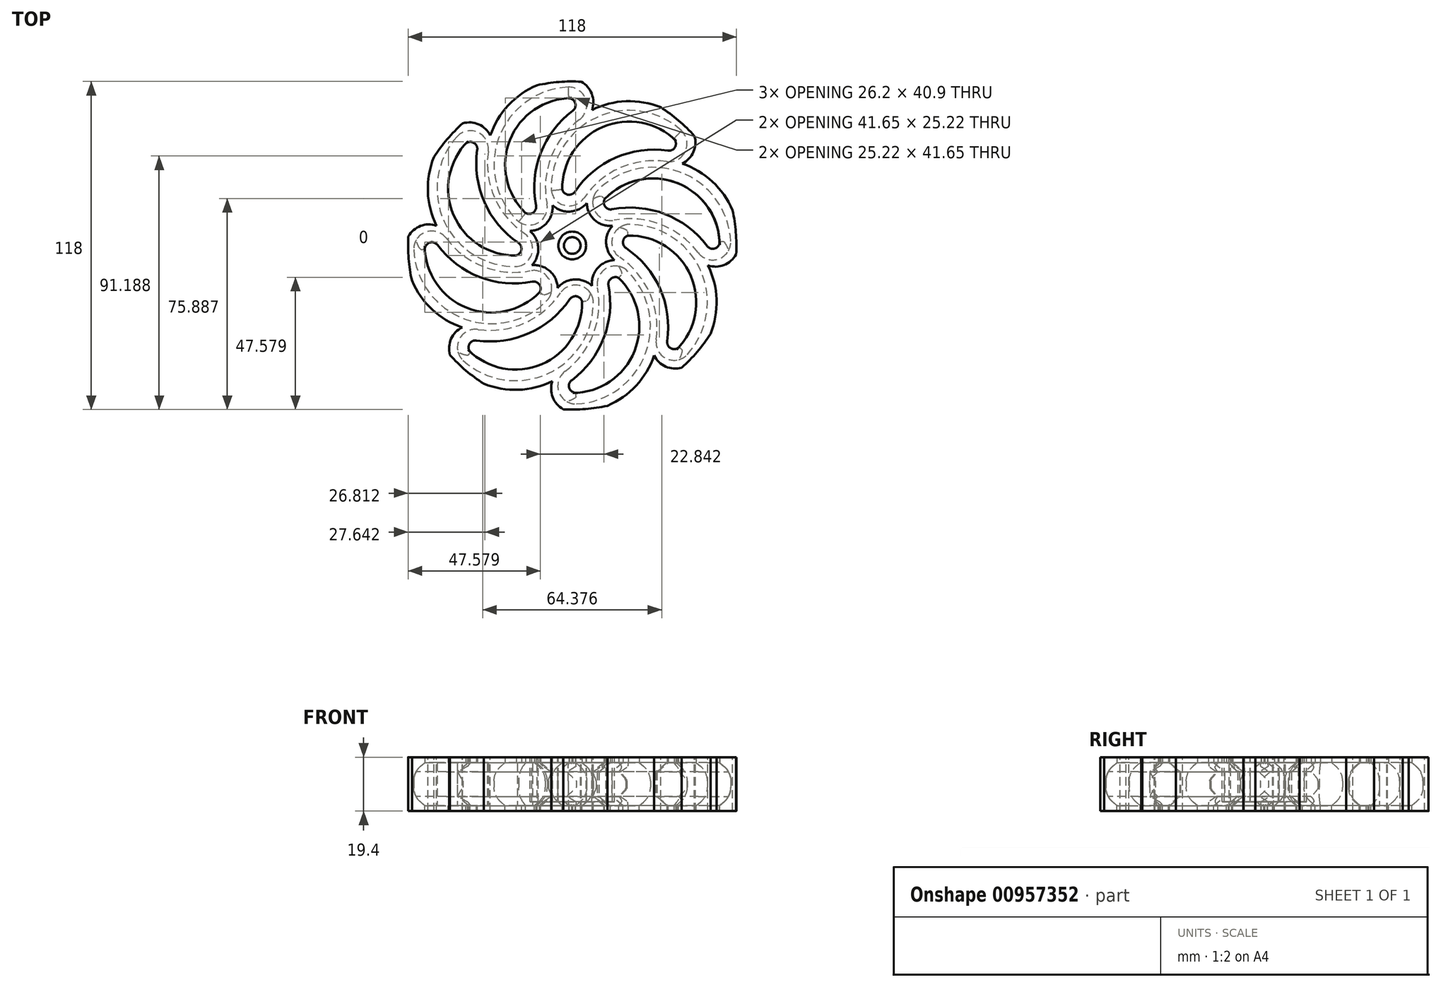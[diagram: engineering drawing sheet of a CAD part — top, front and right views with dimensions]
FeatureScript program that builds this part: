
annotation { "Feature Type Name" : "Feature", "Feature Type Description" : "" }
export const myFeature = defineFeature(function(context is Context, id is Id, definition is map)
    precondition{}
    {
        {
            var Q0;
            Q0=qCreatedBy(makeId("Top.planeOp"),FACE);
            var sketch = newSketch(context, id + "F0", { "sketchPlane" : qUnion([Q0])});
            skCircle(sketch, "E0", {"center": v(0, 0) * mm, "radius": 59 * mm});
            skCircle(sketch, "E1", {"center": v(0, 0) * mm, "radius": 1.5 * mm});
            skLineSegment(sketch, "E2", {"start": v(0, 0) * mm, "end": v(41.72, 41.72) * mm, "construction": true});
            skArc(sketch, "E3", {"start": v(41.72, 41.72) * mm, "mid": v(0, 41.72) * mm, "end": v(0, 0) * mm, "construction": true});
            skCircle(sketch, "E4.0", {"center": v(0, 0) * mm, "radius": 57 * mm});
            skArc(sketch, "E5.0", {"start": v(25.42, 51.02) * mm, "mid": v(-6.1, 35.12) * mm, "end": v(-1.5, 0.11) * mm});
            skArc(sketch, "E6.0", {"start": v(32.3, 46.96) * mm, "mid": v(-2.36, 37.39) * mm, "end": v(-0.05, 1.5) * mm});
            skArc(sketch, "E7.1.0", {"start": v(-18.1, 54.05) * mm, "mid": v(-29.15, 20.52) * mm, "end": v(-1.14, -0.98) * mm});
            skArc(sketch, "E7.1.1", {"start": v(-10.36, 56.05) * mm, "mid": v(-28.1, 24.77) * mm, "end": v(-1.1, 1.02) * mm});
            skArc(sketch, "E7.2.0", {"start": v(-51.02, 25.42) * mm, "mid": v(-35.12, -6.1) * mm, "end": v(-0.11, -1.5) * mm});
            skArc(sketch, "E7.2.1", {"start": v(-46.96, 32.3) * mm, "mid": v(-37.39, -2.36) * mm, "end": v(-1.5, -0.05) * mm});
            skArc(sketch, "E7.3.0", {"start": v(-54.05, -18.1) * mm, "mid": v(-20.52, -29.15) * mm, "end": v(0.98, -1.14) * mm});
            skArc(sketch, "E7.3.1", {"start": v(-56.05, -10.36) * mm, "mid": v(-24.77, -28.1) * mm, "end": v(-1.02, -1.1) * mm});
            skArc(sketch, "E7.4.0", {"start": v(-25.42, -51.02) * mm, "mid": v(6.1, -35.12) * mm, "end": v(1.5, -0.11) * mm});
            skArc(sketch, "E7.4.1", {"start": v(-32.3, -46.96) * mm, "mid": v(2.36, -37.39) * mm, "end": v(0.05, -1.5) * mm});
            skArc(sketch, "E7.5.0", {"start": v(18.1, -54.05) * mm, "mid": v(29.15, -20.52) * mm, "end": v(1.14, 0.98) * mm});
            skArc(sketch, "E7.5.1", {"start": v(10.36, -56.05) * mm, "mid": v(28.1, -24.77) * mm, "end": v(1.1, -1.02) * mm});
            skArc(sketch, "E7.6.0", {"start": v(51.02, -25.42) * mm, "mid": v(35.12, 6.1) * mm, "end": v(0.11, 1.5) * mm});
            skArc(sketch, "E7.6.1", {"start": v(46.96, -32.3) * mm, "mid": v(37.39, 2.36) * mm, "end": v(1.5, 0.05) * mm});
            skArc(sketch, "E7.7.0", {"start": v(54.05, 18.1) * mm, "mid": v(20.52, 29.15) * mm, "end": v(-0.98, 1.14) * mm});
            skArc(sketch, "E7.7.1", {"start": v(56.05, 10.36) * mm, "mid": v(24.77, 28.1) * mm, "end": v(1.02, 1.1) * mm});
            skSolve(sketch);
        }
        {
            var Q0;
            {var subQ7=sQuery(id+"F0.wireOp",EDGE,"E7.1.1");var subQ9=sQuery(id+"F0.wireOp",EDGE,"E1");var subQ10=makeQuery(id+"F0.imprint","INTERSECT",VERTEX,{"derivedFrom":[subQ9,subQ7]});Q0=makeQuery(id+"F0.imprint","IMPRINT",FACE,{"disambiguationData":[TD([[makeQuery(id+"F0.imprint","IMPRINT",EDGE,{"disambiguationData":[TD([[subQ10,1.0]])],"derivedFrom":subQ9}),-1.0]])]});}
            var Q1;
            {var subQ1=sQuery(id+"F0.wireOp",EDGE,"E1");var subQ5=sQuery(id+"F0.wireOp",EDGE,"E6.0");var subQ6=makeQuery(id+"F0.imprint","INTERSECT",VERTEX,{"derivedFrom":[subQ1,subQ5]});Q1=makeQuery(id+"F0.imprint","IMPRINT",FACE,{"disambiguationData":[TD([[makeQuery(id+"F0.imprint","IMPRINT",EDGE,{"disambiguationData":[TD([[subQ6,1.0]])],"derivedFrom":subQ1}),-1.0]])]});}
            var Q2;
            {var subQ0=sQuery(id+"F0.wireOp",EDGE,"E7.5.0");var subQ1=sQuery(id+"F0.wireOp",EDGE,"E1");var subQ2=makeQuery(id+"F0.imprint","INTERSECT",VERTEX,{"derivedFrom":[subQ1,subQ0]});Q2=makeQuery(id+"F0.imprint","IMPRINT",FACE,{"disambiguationData":[TD([[makeQuery(id+"F0.imprint","IMPRINT",EDGE,{"disambiguationData":[TD([[subQ2,-1.0]])],"derivedFrom":subQ1}),-1.0]])]});}
            var Q3;
            {var subQ5=sQuery(id+"F0.wireOp",EDGE,"E7.4.0");var subQ6=sQuery(id+"F0.wireOp",EDGE,"E1");var subQ7=makeQuery(id+"F0.imprint","INTERSECT",VERTEX,{"derivedFrom":[subQ6,subQ5]});Q3=makeQuery(id+"F0.imprint","IMPRINT",FACE,{"disambiguationData":[TD([[makeQuery(id+"F0.imprint","IMPRINT",EDGE,{"disambiguationData":[TD([[subQ7,-1.0]])],"derivedFrom":subQ6}),-1.0]])]});}
            var Q4;
            {var subQ0=sQuery(id+"F0.wireOp",EDGE,"E7.3.0");var subQ1=sQuery(id+"F0.wireOp",EDGE,"E1");var subQ2=makeQuery(id+"F0.imprint","INTERSECT",VERTEX,{"derivedFrom":[subQ1,subQ0]});Q4=makeQuery(id+"F0.imprint","IMPRINT",FACE,{"disambiguationData":[TD([[makeQuery(id+"F0.imprint","IMPRINT",EDGE,{"disambiguationData":[TD([[subQ2,-1.0]])],"derivedFrom":subQ1}),-1.0]])]});}
            var Q5;
            {var subQ5=sQuery(id+"F0.wireOp",EDGE,"E7.2.0");var subQ6=sQuery(id+"F0.wireOp",EDGE,"E1");var subQ7=makeQuery(id+"F0.imprint","INTERSECT",VERTEX,{"derivedFrom":[subQ6,subQ5]});Q5=makeQuery(id+"F0.imprint","IMPRINT",FACE,{"disambiguationData":[TD([[makeQuery(id+"F0.imprint","IMPRINT",EDGE,{"disambiguationData":[TD([[subQ7,-1.0]])],"derivedFrom":subQ6}),-1.0]])]});}
            var Q6;
            {var subQ5=sQuery(id+"F0.wireOp",EDGE,"E7.1.0");var subQ6=sQuery(id+"F0.wireOp",EDGE,"E1");var subQ7=makeQuery(id+"F0.imprint","INTERSECT",VERTEX,{"derivedFrom":[subQ6,subQ5]});Q6=makeQuery(id+"F0.imprint","IMPRINT",FACE,{"disambiguationData":[TD([[makeQuery(id+"F0.imprint","IMPRINT",EDGE,{"disambiguationData":[TD([[subQ7,-1.0]])],"derivedFrom":subQ6}),-1.0]])]});}
            var Q7;
            {var subQ5=sQuery(id+"F0.wireOp",EDGE,"E5.0");var subQ6=sQuery(id+"F0.wireOp",EDGE,"E1");var subQ7=makeQuery(id+"F0.imprint","INTERSECT",VERTEX,{"derivedFrom":[subQ6,subQ5]});Q7=makeQuery(id+"F0.imprint","IMPRINT",FACE,{"disambiguationData":[TD([[makeQuery(id+"F0.imprint","IMPRINT",EDGE,{"disambiguationData":[TD([[subQ7,-1.0]])],"derivedFrom":subQ6}),-1.0]])]});}
            var Q8;
            {var subQ0=sQuery(id+"F0.wireOp",EDGE,"E5.0");var subQ1=sQuery(id+"F0.wireOp",EDGE,"E1");var subQ2=makeQuery(id+"F0.imprint","INTERSECT",VERTEX,{"derivedFrom":[subQ1,subQ0]});Q8=makeQuery(id+"F0.imprint","IMPRINT",FACE,{"disambiguationData":[TD([[makeQuery(id+"F0.imprint","IMPRINT",EDGE,{"disambiguationData":[TD([[subQ2,1.0]])],"derivedFrom":subQ1}),-1.0]])]});}
            var Q9;
            {var subQ0=sQuery(id+"F0.wireOp",EDGE,"E6.0");var subQ1=sQuery(id+"F0.wireOp",EDGE,"E1");var subQ2=makeQuery(id+"F0.imprint","INTERSECT",VERTEX,{"derivedFrom":[subQ1,subQ0]});Q9=makeQuery(id+"F0.imprint","IMPRINT",FACE,{"disambiguationData":[TD([[makeQuery(id+"F0.imprint","IMPRINT",EDGE,{"disambiguationData":[TD([[subQ2,-1.0]])],"derivedFrom":subQ1}),-1.0]])]});}
            var Q10;
            {var subQ0=sQuery(id+"F0.wireOp",EDGE,"E7.6.0");var subQ1=sQuery(id+"F0.wireOp",EDGE,"E1");var subQ2=makeQuery(id+"F0.imprint","INTERSECT",VERTEX,{"derivedFrom":[subQ1,subQ0]});Q10=makeQuery(id+"F0.imprint","IMPRINT",FACE,{"disambiguationData":[TD([[makeQuery(id+"F0.imprint","IMPRINT",EDGE,{"disambiguationData":[TD([[subQ2,1.0]])],"derivedFrom":subQ1}),-1.0]])]});}
            var Q11;
            {var subQ0=sQuery(id+"F0.wireOp",EDGE,"E7.5.0");var subQ1=sQuery(id+"F0.wireOp",EDGE,"E1");var subQ2=makeQuery(id+"F0.imprint","INTERSECT",VERTEX,{"derivedFrom":[subQ1,subQ0]});Q11=makeQuery(id+"F0.imprint","IMPRINT",FACE,{"disambiguationData":[TD([[makeQuery(id+"F0.imprint","IMPRINT",EDGE,{"disambiguationData":[TD([[subQ2,1.0]])],"derivedFrom":subQ1}),-1.0]])]});}
            var Q12;
            {var subQ0=sQuery(id+"F0.wireOp",EDGE,"E7.4.0");var subQ1=sQuery(id+"F0.wireOp",EDGE,"E1");var subQ2=makeQuery(id+"F0.imprint","INTERSECT",VERTEX,{"derivedFrom":[subQ1,subQ0]});Q12=makeQuery(id+"F0.imprint","IMPRINT",FACE,{"disambiguationData":[TD([[makeQuery(id+"F0.imprint","IMPRINT",EDGE,{"disambiguationData":[TD([[subQ2,1.0]])],"derivedFrom":subQ1}),-1.0]])]});}
            var Q13;
            {var subQ0=sQuery(id+"F0.wireOp",EDGE,"E7.3.0");var subQ1=sQuery(id+"F0.wireOp",EDGE,"E1");var subQ2=makeQuery(id+"F0.imprint","INTERSECT",VERTEX,{"derivedFrom":[subQ1,subQ0]});Q13=makeQuery(id+"F0.imprint","IMPRINT",FACE,{"disambiguationData":[TD([[makeQuery(id+"F0.imprint","IMPRINT",EDGE,{"disambiguationData":[TD([[subQ2,1.0]])],"derivedFrom":subQ1}),-1.0]])]});}
            var Q14;
            {var subQ0=sQuery(id+"F0.wireOp",EDGE,"E7.2.0");var subQ1=sQuery(id+"F0.wireOp",EDGE,"E1");var subQ2=makeQuery(id+"F0.imprint","INTERSECT",VERTEX,{"derivedFrom":[subQ1,subQ0]});Q14=makeQuery(id+"F0.imprint","IMPRINT",FACE,{"disambiguationData":[TD([[makeQuery(id+"F0.imprint","IMPRINT",EDGE,{"disambiguationData":[TD([[subQ2,1.0]])],"derivedFrom":subQ1}),-1.0]])]});}
            var Q15;
            {var subQ0=sQuery(id+"F0.wireOp",EDGE,"E7.1.0");var subQ1=sQuery(id+"F0.wireOp",EDGE,"E1");var subQ2=makeQuery(id+"F0.imprint","INTERSECT",VERTEX,{"derivedFrom":[subQ1,subQ0]});Q15=makeQuery(id+"F0.imprint","IMPRINT",FACE,{"disambiguationData":[TD([[makeQuery(id+"F0.imprint","IMPRINT",EDGE,{"disambiguationData":[TD([[subQ2,1.0]])],"derivedFrom":subQ1}),-1.0]])]});}
            var Q16;
            Q16=makeQuery(id+"F0.imprint","IMPRINT",FACE,{"disambiguationData":[TD([[makeQuery(id+"F0.imprint","IMPRINT",EDGE,{"derivedFrom":sQuery(id+"F0.wireOp",EDGE,"E0")}),1.0]])]});
            extrude(context, id + "F1", {"entities" : qUnion([Q0, Q1, Q2, Q3, Q4, Q5, Q6, Q7, Q8, Q9, Q10, Q11, Q12, Q13, Q14, Q15, Q16]), "depth" : 3.1 * mm, "offsetDistance" : 25 * mm, "hasSecondDirection" : true, "secondDirectionOppositeDirection" : true, "secondDirectionDepth" : .4 * mm});
        }
        {
            var Q0;
            Q0=makeQuery(id+"F1.opExtrude","SWEPT_EDGE",EDGE,{"disambiguationData":[OSD([sQuery(id+"F0.wireOp",EDGE,"E7.4.0"),sQuery(id+"F0.wireOp",EDGE,"E7.5.1")])]});
            var Q1;
            Q1=makeQuery(id+"F1.opExtrude","SWEPT_EDGE",EDGE,{"disambiguationData":[OSD([sQuery(id+"F0.wireOp",EDGE,"E7.5.0"),sQuery(id+"F0.wireOp",EDGE,"E7.6.1")])]});
            var Q2;
            Q2=makeQuery(id+"F1.opExtrude","SWEPT_EDGE",EDGE,{"disambiguationData":[OSD([sQuery(id+"F0.wireOp",EDGE,"E7.6.0"),sQuery(id+"F0.wireOp",EDGE,"E7.7.1")])]});
            var Q3;
            Q3=makeQuery(id+"F1.opExtrude","SWEPT_EDGE",EDGE,{"disambiguationData":[OSD([sQuery(id+"F0.wireOp",EDGE,"E6.0"),sQuery(id+"F0.wireOp",EDGE,"E7.7.0")])]});
            var Q4;
            Q4=makeQuery(id+"F1.opExtrude","SWEPT_EDGE",EDGE,{"disambiguationData":[OSD([sQuery(id+"F0.wireOp",EDGE,"E7.1.0"),sQuery(id+"F0.wireOp",EDGE,"E7.2.1")])]});
            var Q5;
            Q5=makeQuery(id+"F1.opExtrude","SWEPT_EDGE",EDGE,{"disambiguationData":[OSD([sQuery(id+"F0.wireOp",EDGE,"E7.2.0"),sQuery(id+"F0.wireOp",EDGE,"E7.3.1")])]});
            var Q6;
            Q6=makeQuery(id+"F1.opExtrude","SWEPT_EDGE",EDGE,{"disambiguationData":[OSD([sQuery(id+"F0.wireOp",EDGE,"E7.3.0"),sQuery(id+"F0.wireOp",EDGE,"E7.4.1")])]});
            var Q7;
            Q7=makeQuery(id+"F1.opExtrude","SWEPT_EDGE",EDGE,{"disambiguationData":[OSD([sQuery(id+"F0.wireOp",EDGE,"E5.0"),sQuery(id+"F0.wireOp",EDGE,"E7.1.1")])]});
            fillet(context, id + "F2", {"entities" : qUnion([Q0, Q1, Q2, Q3, Q4, Q5, Q6, Q7]), "radius" : 6.5 * mm, "tangentPropagation" : true, "allowEdgeOverflow" : false});
        }
        {
            var Q0;
            Q0=makeQuery(id+"F1.opExtrude","SWEPT_EDGE",EDGE,{"disambiguationData":[OSD([sQuery(id+"F0.wireOp",EDGE,"E4.0"),sQuery(id+"F0.wireOp",EDGE,"E7.4.0")])]});
            var Q1;
            Q1=makeQuery(id+"F1.opExtrude","SWEPT_EDGE",EDGE,{"disambiguationData":[OSD([sQuery(id+"F0.wireOp",EDGE,"E4.0"),sQuery(id+"F0.wireOp",EDGE,"E7.3.0")])]});
            var Q2;
            Q2=makeQuery(id+"F1.opExtrude","SWEPT_EDGE",EDGE,{"disambiguationData":[OSD([sQuery(id+"F0.wireOp",EDGE,"E4.0"),sQuery(id+"F0.wireOp",EDGE,"E7.2.0")])]});
            var Q3;
            Q3=makeQuery(id+"F1.opExtrude","SWEPT_EDGE",EDGE,{"disambiguationData":[OSD([sQuery(id+"F0.wireOp",EDGE,"E4.0"),sQuery(id+"F0.wireOp",EDGE,"E7.1.0")])]});
            var Q4;
            Q4=makeQuery(id+"F1.opExtrude","SWEPT_EDGE",EDGE,{"disambiguationData":[OSD([sQuery(id+"F0.wireOp",EDGE,"E4.0"),sQuery(id+"F0.wireOp",EDGE,"E5.0")])]});
            var Q5;
            Q5=makeQuery(id+"F1.opExtrude","SWEPT_EDGE",EDGE,{"disambiguationData":[OSD([sQuery(id+"F0.wireOp",EDGE,"E4.0"),sQuery(id+"F0.wireOp",EDGE,"E7.7.0")])]});
            var Q6;
            Q6=makeQuery(id+"F1.opExtrude","SWEPT_EDGE",EDGE,{"disambiguationData":[OSD([sQuery(id+"F0.wireOp",EDGE,"E4.0"),sQuery(id+"F0.wireOp",EDGE,"E7.6.0")])]});
            var Q7;
            Q7=makeQuery(id+"F1.opExtrude","SWEPT_EDGE",EDGE,{"disambiguationData":[OSD([sQuery(id+"F0.wireOp",EDGE,"E4.0"),sQuery(id+"F0.wireOp",EDGE,"E7.5.0")])]});
            fillet(context, id + "F3", {"entities" : qUnion([Q0, Q1, Q2, Q3, Q4, Q5, Q6, Q7]), "radius" : 6.5 * mm, "tangentPropagation" : true, "allowEdgeOverflow" : false});
        }
        {
            var Q0;
            Q0=makeQuery(id+"F1.opExtrude","SWEPT_EDGE",EDGE,{"disambiguationData":[OSD([sQuery(id+"F0.wireOp",EDGE,"E4.0"),sQuery(id+"F0.wireOp",EDGE,"E7.2.1")])]});
            var Q1;
            Q1=makeQuery(id+"F1.opExtrude","SWEPT_EDGE",EDGE,{"disambiguationData":[OSD([sQuery(id+"F0.wireOp",EDGE,"E4.0"),sQuery(id+"F0.wireOp",EDGE,"E7.1.1")])]});
            var Q2;
            Q2=makeQuery(id+"F1.opExtrude","SWEPT_EDGE",EDGE,{"disambiguationData":[OSD([sQuery(id+"F0.wireOp",EDGE,"E4.0"),sQuery(id+"F0.wireOp",EDGE,"E6.0")])]});
            var Q3;
            Q3=makeQuery(id+"F1.opExtrude","SWEPT_EDGE",EDGE,{"disambiguationData":[OSD([sQuery(id+"F0.wireOp",EDGE,"E4.0"),sQuery(id+"F0.wireOp",EDGE,"E7.3.1")])]});
            var Q4;
            Q4=makeQuery(id+"F1.opExtrude","SWEPT_EDGE",EDGE,{"disambiguationData":[OSD([sQuery(id+"F0.wireOp",EDGE,"E4.0"),sQuery(id+"F0.wireOp",EDGE,"E7.4.1")])]});
            var Q5;
            Q5=makeQuery(id+"F1.opExtrude","SWEPT_EDGE",EDGE,{"disambiguationData":[OSD([sQuery(id+"F0.wireOp",EDGE,"E4.0"),sQuery(id+"F0.wireOp",EDGE,"E7.5.1")])]});
            var Q6;
            Q6=makeQuery(id+"F1.opExtrude","SWEPT_EDGE",EDGE,{"disambiguationData":[OSD([sQuery(id+"F0.wireOp",EDGE,"E4.0"),sQuery(id+"F0.wireOp",EDGE,"E7.6.1")])]});
            var Q7;
            Q7=makeQuery(id+"F1.opExtrude","SWEPT_EDGE",EDGE,{"disambiguationData":[OSD([sQuery(id+"F0.wireOp",EDGE,"E4.0"),sQuery(id+"F0.wireOp",EDGE,"E7.7.1")])]});
            fillet(context, id + "F4", {"entities" : qUnion([Q0, Q1, Q2, Q3, Q4, Q5, Q6, Q7]), "radius" : 28 * mm, "tangentPropagation" : true, "allowEdgeOverflow" : false});
        }
        {
            var Q0;
            Q0=makeQuery(id+"F1.opExtrude","CAP_FACE",FACE,{"disambiguationData":[OSD([sQuery(id+"F0.wireOp",EDGE,"E0"),sQuery(id+"F0.wireOp",EDGE,"E1"),sQuery(id+"F0.wireOp",EDGE,"E4.0"),sQuery(id+"F0.wireOp",EDGE,"E5.0"),sQuery(id+"F0.wireOp",EDGE,"E6.0"),sQuery(id+"F0.wireOp",EDGE,"E7.1.0"),sQuery(id+"F0.wireOp",EDGE,"E7.1.1"),sQuery(id+"F0.wireOp",EDGE,"E7.2.0"),sQuery(id+"F0.wireOp",EDGE,"E7.2.1"),sQuery(id+"F0.wireOp",EDGE,"E7.3.0"),sQuery(id+"F0.wireOp",EDGE,"E7.3.1"),sQuery(id+"F0.wireOp",EDGE,"E7.4.0"),sQuery(id+"F0.wireOp",EDGE,"E7.4.1"),sQuery(id+"F0.wireOp",EDGE,"E7.5.0"),sQuery(id+"F0.wireOp",EDGE,"E7.5.1"),sQuery(id+"F0.wireOp",EDGE,"E7.6.0"),sQuery(id+"F0.wireOp",EDGE,"E7.6.1"),sQuery(id+"F0.wireOp",EDGE,"E7.7.0"),sQuery(id+"F0.wireOp",EDGE,"E7.7.1")])],"isStart":false});
            cPlane(context, id + "F5", {"entities" : qUnion([Q0]), "cplaneType" : CPlaneType.OFFSET, "offset" : 4.2 * mm, "width" : 150 * mm, "height" : 150 * mm});
        }
        {
            var Q0;
            Q0=qCreatedBy(id+"F5.planeOp",FACE);
            var sketch = newSketch(context, id + "F6", { "sketchPlane" : qUnion([Q0])});
            skCircle(sketch, "E8.0", {"center": v(0, 0) * mm, "radius": 59 * mm});
            skArc(sketch, "E9.0", {"start": v(-1.1, 52.97) * mm, "mid": v(-0.66, 53) * mm, "end": v(-0.21, 53.01) * mm});
            skArc(sketch, "E9.1", {"start": v(-16.75, 11.7) * mm, "mid": v(-22.4, 37.93) * mm, "end": v(-0.21, 53.01) * mm});
            skArc(sketch, "E9.2", {"start": v(-1.1, 52.97) * mm, "mid": v(1.1, 51.17) * mm, "end": v(0.19, 48.48) * mm});
            skArc(sketch, "E9.3", {"start": v(0.19, 48.48) * mm, "mid": v(-11.32, 33.3) * mm, "end": v(-13.02, 14.33) * mm});
            skArc(sketch, "E9.4", {"start": v(-13.02, 14.33) * mm, "mid": v(-14.03, 11.82) * mm, "end": v(-16.75, 11.7) * mm});
            skCircle(sketch, "E10.0", {"center": v(0, 0) * mm, "radius": 1.5 * mm});
            skArc(sketch, "E11.1.0", {"start": v(-20.12, -3.56) * mm, "mid": v(-42.66, 10.99) * mm, "end": v(-37.64, 37.34) * mm});
            skArc(sketch, "E11.1.1", {"start": v(-38.24, 36.68) * mm, "mid": v(-37.94, 37) * mm, "end": v(-37.64, 37.34) * mm});
            skArc(sketch, "E11.1.2", {"start": v(-38.24, 36.68) * mm, "mid": v(-35.41, 36.96) * mm, "end": v(-34.15, 34.42) * mm});
            skArc(sketch, "E11.1.3", {"start": v(-34.15, 34.42) * mm, "mid": v(-31.55, 15.55) * mm, "end": v(-19.34, 0.93) * mm});
            skArc(sketch, "E11.1.4", {"start": v(-19.34, 0.93) * mm, "mid": v(-18.28, -1.57) * mm, "end": v(-20.12, -3.56) * mm});
            skArc(sketch, "E11.2.0", {"start": v(-11.7, -16.75) * mm, "mid": v(-37.93, -22.4) * mm, "end": v(-53.01, -0.21) * mm});
            skArc(sketch, "E11.2.1", {"start": v(-52.97, -1.1) * mm, "mid": v(-53, -0.66) * mm, "end": v(-53.01, -0.21) * mm});
            skArc(sketch, "E11.2.2", {"start": v(-52.97, -1.1) * mm, "mid": v(-51.17, 1.1) * mm, "end": v(-48.48, 0.19) * mm});
            skArc(sketch, "E11.2.3", {"start": v(-48.48, 0.19) * mm, "mid": v(-33.3, -11.32) * mm, "end": v(-14.33, -13.02) * mm});
            skArc(sketch, "E11.2.4", {"start": v(-14.33, -13.02) * mm, "mid": v(-11.82, -14.03) * mm, "end": v(-11.7, -16.75) * mm});
            skArc(sketch, "E11.3.0", {"start": v(3.56, -20.12) * mm, "mid": v(-10.99, -42.66) * mm, "end": v(-37.34, -37.64) * mm});
            skArc(sketch, "E11.3.1", {"start": v(-36.68, -38.24) * mm, "mid": v(-37, -37.94) * mm, "end": v(-37.34, -37.64) * mm});
            skArc(sketch, "E11.3.2", {"start": v(-36.68, -38.24) * mm, "mid": v(-36.96, -35.41) * mm, "end": v(-34.42, -34.15) * mm});
            skArc(sketch, "E11.3.3", {"start": v(-34.42, -34.15) * mm, "mid": v(-15.55, -31.55) * mm, "end": v(-0.93, -19.34) * mm});
            skArc(sketch, "E11.3.4", {"start": v(-0.93, -19.34) * mm, "mid": v(1.57, -18.28) * mm, "end": v(3.56, -20.12) * mm});
            skArc(sketch, "E11.4.0", {"start": v(16.75, -11.7) * mm, "mid": v(22.4, -37.93) * mm, "end": v(0.21, -53.01) * mm});
            skArc(sketch, "E11.4.1", {"start": v(1.1, -52.97) * mm, "mid": v(0.66, -53) * mm, "end": v(0.21, -53.01) * mm});
            skArc(sketch, "E11.4.2", {"start": v(1.1, -52.97) * mm, "mid": v(-1.1, -51.17) * mm, "end": v(-0.19, -48.48) * mm});
            skArc(sketch, "E11.4.3", {"start": v(-0.19, -48.48) * mm, "mid": v(11.32, -33.3) * mm, "end": v(13.02, -14.33) * mm});
            skArc(sketch, "E11.4.4", {"start": v(13.02, -14.33) * mm, "mid": v(14.03, -11.82) * mm, "end": v(16.75, -11.7) * mm});
            skArc(sketch, "E11.5.0", {"start": v(20.12, 3.56) * mm, "mid": v(42.66, -10.99) * mm, "end": v(37.64, -37.34) * mm});
            skArc(sketch, "E11.5.1", {"start": v(38.24, -36.68) * mm, "mid": v(37.94, -37) * mm, "end": v(37.64, -37.34) * mm});
            skArc(sketch, "E11.5.2", {"start": v(38.24, -36.68) * mm, "mid": v(35.41, -36.96) * mm, "end": v(34.15, -34.42) * mm});
            skArc(sketch, "E11.5.3", {"start": v(34.15, -34.42) * mm, "mid": v(31.55, -15.55) * mm, "end": v(19.34, -0.93) * mm});
            skArc(sketch, "E11.5.4", {"start": v(19.34, -0.93) * mm, "mid": v(18.28, 1.57) * mm, "end": v(20.12, 3.56) * mm});
            skArc(sketch, "E11.6.0", {"start": v(11.7, 16.75) * mm, "mid": v(37.93, 22.4) * mm, "end": v(53.01, 0.21) * mm});
            skArc(sketch, "E11.6.1", {"start": v(52.97, 1.1) * mm, "mid": v(53, 0.66) * mm, "end": v(53.01, 0.21) * mm});
            skArc(sketch, "E11.6.2", {"start": v(52.97, 1.1) * mm, "mid": v(51.17, -1.1) * mm, "end": v(48.48, -0.19) * mm});
            skArc(sketch, "E11.6.3", {"start": v(48.48, -0.19) * mm, "mid": v(33.3, 11.32) * mm, "end": v(14.33, 13.02) * mm});
            skArc(sketch, "E11.6.4", {"start": v(14.33, 13.02) * mm, "mid": v(11.82, 14.03) * mm, "end": v(11.7, 16.75) * mm});
            skArc(sketch, "E11.7.0", {"start": v(-3.56, 20.12) * mm, "mid": v(10.99, 42.66) * mm, "end": v(37.34, 37.64) * mm});
            skArc(sketch, "E11.7.1", {"start": v(36.68, 38.24) * mm, "mid": v(37, 37.94) * mm, "end": v(37.34, 37.64) * mm});
            skArc(sketch, "E11.7.2", {"start": v(36.68, 38.24) * mm, "mid": v(36.96, 35.41) * mm, "end": v(34.42, 34.15) * mm});
            skArc(sketch, "E11.7.3", {"start": v(34.42, 34.15) * mm, "mid": v(15.55, 31.55) * mm, "end": v(0.93, 19.34) * mm});
            skArc(sketch, "E11.7.4", {"start": v(0.93, 19.34) * mm, "mid": v(-1.57, 18.28) * mm, "end": v(-3.56, 20.12) * mm});
            skSolve(sketch);
        }
        {
            var Q0;
            Q0 = qSketchRegion(id + "F6", true);
            var Q1;
            Q1=makeQuery(id+"F1.opExtrude","CAP_FACE",FACE,{"disambiguationData":[OSD([sQuery(id+"F0.wireOp",EDGE,"E0"),sQuery(id+"F0.wireOp",EDGE,"E1"),sQuery(id+"F0.wireOp",EDGE,"E4.0"),sQuery(id+"F0.wireOp",EDGE,"E5.0"),sQuery(id+"F0.wireOp",EDGE,"E6.0"),sQuery(id+"F0.wireOp",EDGE,"E7.1.0"),sQuery(id+"F0.wireOp",EDGE,"E7.1.1"),sQuery(id+"F0.wireOp",EDGE,"E7.2.0"),sQuery(id+"F0.wireOp",EDGE,"E7.2.1"),sQuery(id+"F0.wireOp",EDGE,"E7.3.0"),sQuery(id+"F0.wireOp",EDGE,"E7.3.1"),sQuery(id+"F0.wireOp",EDGE,"E7.4.0"),sQuery(id+"F0.wireOp",EDGE,"E7.4.1"),sQuery(id+"F0.wireOp",EDGE,"E7.5.0"),sQuery(id+"F0.wireOp",EDGE,"E7.5.1"),sQuery(id+"F0.wireOp",EDGE,"E7.6.0"),sQuery(id+"F0.wireOp",EDGE,"E7.6.1"),sQuery(id+"F0.wireOp",EDGE,"E7.7.0"),sQuery(id+"F0.wireOp",EDGE,"E7.7.1")])],"isStart":false});
            var Q2;
            Q2=makeQuery(id+"F1.opExtrude","SWEPT_BODY",BODY,{"disambiguationData":[OSD([sQuery(id+"F0.wireOp",EDGE,"E0"),sQuery(id+"F0.wireOp",EDGE,"E1"),sQuery(id+"F0.wireOp",EDGE,"E4.0"),sQuery(id+"F0.wireOp",EDGE,"E5.0"),sQuery(id+"F0.wireOp",EDGE,"E6.0"),sQuery(id+"F0.wireOp",EDGE,"E7.1.0"),sQuery(id+"F0.wireOp",EDGE,"E7.1.1"),sQuery(id+"F0.wireOp",EDGE,"E7.2.0"),sQuery(id+"F0.wireOp",EDGE,"E7.2.1"),sQuery(id+"F0.wireOp",EDGE,"E7.3.0"),sQuery(id+"F0.wireOp",EDGE,"E7.3.1"),sQuery(id+"F0.wireOp",EDGE,"E7.4.0"),sQuery(id+"F0.wireOp",EDGE,"E7.4.1"),sQuery(id+"F0.wireOp",EDGE,"E7.5.0"),sQuery(id+"F0.wireOp",EDGE,"E7.5.1"),sQuery(id+"F0.wireOp",EDGE,"E7.6.0"),sQuery(id+"F0.wireOp",EDGE,"E7.6.1"),sQuery(id+"F0.wireOp",EDGE,"E7.7.0"),sQuery(id+"F0.wireOp",EDGE,"E7.7.1")])]});
            extrude(context, id + "F7", {"entities" : qUnion([Q0]), "depth" : 2 * mm, "endBoundEntityFace" : qUnion([Q1]), "endBoundEntityBody" : qUnion([Q2]), "offsetDistance" : 25 * mm});
        }
        {
            var Q0;
            Q0=makeQuery(id+"F1.opExtrude","CAP_FACE",FACE,{"disambiguationData":[OSD([sQuery(id+"F0.wireOp",EDGE,"E0"),sQuery(id+"F0.wireOp",EDGE,"E1"),sQuery(id+"F0.wireOp",EDGE,"E4.0"),sQuery(id+"F0.wireOp",EDGE,"E5.0"),sQuery(id+"F0.wireOp",EDGE,"E6.0"),sQuery(id+"F0.wireOp",EDGE,"E7.1.0"),sQuery(id+"F0.wireOp",EDGE,"E7.1.1"),sQuery(id+"F0.wireOp",EDGE,"E7.2.0"),sQuery(id+"F0.wireOp",EDGE,"E7.2.1"),sQuery(id+"F0.wireOp",EDGE,"E7.3.0"),sQuery(id+"F0.wireOp",EDGE,"E7.3.1"),sQuery(id+"F0.wireOp",EDGE,"E7.4.0"),sQuery(id+"F0.wireOp",EDGE,"E7.4.1"),sQuery(id+"F0.wireOp",EDGE,"E7.5.0"),sQuery(id+"F0.wireOp",EDGE,"E7.5.1"),sQuery(id+"F0.wireOp",EDGE,"E7.6.0"),sQuery(id+"F0.wireOp",EDGE,"E7.6.1"),sQuery(id+"F0.wireOp",EDGE,"E7.7.0"),sQuery(id+"F0.wireOp",EDGE,"E7.7.1")])],"isStart":false});
            extrude(context, id + "F8", {"entities" : qUnion([Q0]), "operationType" : NewBodyOperationType.ADD, "endBound" : BoundingType.UP_TO_NEXT, "depth" : 25 * mm, "offsetDistance" : 25 * mm});
        }
        {
            var Q0;
            {var subQ0=sQuery(id+"F0.wireOp",EDGE,"E7.7.1");var subQ1=sQuery(id+"F0.wireOp",EDGE,"E7.7.0");var subQ2=sQuery(id+"F0.wireOp",EDGE,"E7.6.1");var subQ3=sQuery(id+"F0.wireOp",EDGE,"E7.6.0");var subQ4=sQuery(id+"F0.wireOp",EDGE,"E7.5.1");var subQ5=sQuery(id+"F0.wireOp",EDGE,"E7.5.0");var subQ6=sQuery(id+"F0.wireOp",EDGE,"E7.4.1");var subQ7=sQuery(id+"F0.wireOp",EDGE,"E7.4.0");var subQ8=sQuery(id+"F0.wireOp",EDGE,"E7.3.1");var subQ9=sQuery(id+"F0.wireOp",EDGE,"E7.3.0");var subQ10=sQuery(id+"F0.wireOp",EDGE,"E7.2.1");var subQ11=sQuery(id+"F0.wireOp",EDGE,"E7.2.0");var subQ12=sQuery(id+"F0.wireOp",EDGE,"E7.1.1");var subQ13=sQuery(id+"F0.wireOp",EDGE,"E7.1.0");var subQ14=sQuery(id+"F0.wireOp",EDGE,"E6.0");var subQ15=sQuery(id+"F0.wireOp",EDGE,"E5.0");var subQ16=sQuery(id+"F0.wireOp",EDGE,"E4.0");var subQ17=sQuery(id+"F0.wireOp",EDGE,"E1");var subQ18=sQuery(id+"F0.wireOp",EDGE,"E0");Q0=makeQuery(id+"F8.opExtrude","CAP_EDGE",EDGE,{"disambiguationData":[OSD([subQ18,subQ17,subQ16,subQ15,subQ14,subQ13,subQ12,subQ11,subQ10,subQ9,subQ8,subQ7,subQ6,subQ5,subQ4,subQ3,subQ2,subQ1,subQ0]),TDD([makeQuery(id+"F4.opFillet","BLEND_EDGE",EDGE,{"blendedFrom":[makeQuery(id+"F1.opExtrude","SWEPT_EDGE",EDGE,{"disambiguationData":[OSD([subQ16,subQ4])]}),makeQuery(id+"F1.opExtrude","CAP_FACE",FACE,{"disambiguationData":[OSD([subQ18,subQ17,subQ16,subQ15,subQ14,subQ13,subQ12,subQ11,subQ10,subQ9,subQ8,subQ7,subQ6,subQ5,subQ4,subQ3,subQ2,subQ1,subQ0])],"isStart":false})],"blendedInto":[makeQuery(id+"F1.opExtrude","CAP_FACE",FACE,{"disambiguationData":[OSD([subQ18,subQ17,subQ16,subQ15,subQ14,subQ13,subQ12,subQ11,subQ10,subQ9,subQ8,subQ7,subQ6,subQ5,subQ4,subQ3,subQ2,subQ1,subQ0])],"isStart":false})]})])],"isStart":false});}
            var Q1;
            Q1=makeQuery(id+"F8.opExtrude","CAP_EDGE",EDGE,{"disambiguationData":[OSD([sQuery(id+"F0.wireOp",EDGE,"E7.4.0")])],"isStart":false});
            var Q2;
            Q2=makeQuery(id+"F8.opExtrude","CAP_EDGE",EDGE,{"disambiguationData":[OSD([sQuery(id+"F0.wireOp",EDGE,"E7.5.0")])],"isStart":false});
            var Q3;
            {var subQ0=sQuery(id+"F0.wireOp",EDGE,"E7.7.1");var subQ1=sQuery(id+"F0.wireOp",EDGE,"E7.7.0");var subQ2=sQuery(id+"F0.wireOp",EDGE,"E7.6.1");var subQ3=sQuery(id+"F0.wireOp",EDGE,"E7.6.0");var subQ4=sQuery(id+"F0.wireOp",EDGE,"E7.5.1");var subQ5=sQuery(id+"F0.wireOp",EDGE,"E7.5.0");var subQ6=sQuery(id+"F0.wireOp",EDGE,"E7.4.1");var subQ7=sQuery(id+"F0.wireOp",EDGE,"E7.4.0");var subQ8=sQuery(id+"F0.wireOp",EDGE,"E7.3.1");var subQ9=sQuery(id+"F0.wireOp",EDGE,"E7.3.0");var subQ10=sQuery(id+"F0.wireOp",EDGE,"E7.2.1");var subQ11=sQuery(id+"F0.wireOp",EDGE,"E7.2.0");var subQ12=sQuery(id+"F0.wireOp",EDGE,"E7.1.1");var subQ13=sQuery(id+"F0.wireOp",EDGE,"E7.1.0");var subQ14=sQuery(id+"F0.wireOp",EDGE,"E6.0");var subQ15=sQuery(id+"F0.wireOp",EDGE,"E5.0");var subQ16=sQuery(id+"F0.wireOp",EDGE,"E4.0");var subQ17=sQuery(id+"F0.wireOp",EDGE,"E1");var subQ18=sQuery(id+"F0.wireOp",EDGE,"E0");Q3=makeQuery(id+"F8.opExtrude","CAP_EDGE",EDGE,{"disambiguationData":[OSD([subQ18,subQ17,subQ16,subQ15,subQ14,subQ13,subQ12,subQ11,subQ10,subQ9,subQ8,subQ7,subQ6,subQ5,subQ4,subQ3,subQ2,subQ1,subQ0]),TDD([makeQuery(id+"F4.opFillet","BLEND_EDGE",EDGE,{"blendedFrom":[makeQuery(id+"F1.opExtrude","SWEPT_EDGE",EDGE,{"disambiguationData":[OSD([subQ16,subQ2])]}),makeQuery(id+"F1.opExtrude","CAP_FACE",FACE,{"disambiguationData":[OSD([subQ18,subQ17,subQ16,subQ15,subQ14,subQ13,subQ12,subQ11,subQ10,subQ9,subQ8,subQ7,subQ6,subQ5,subQ4,subQ3,subQ2,subQ1,subQ0])],"isStart":false})],"blendedInto":[makeQuery(id+"F1.opExtrude","CAP_FACE",FACE,{"disambiguationData":[OSD([subQ18,subQ17,subQ16,subQ15,subQ14,subQ13,subQ12,subQ11,subQ10,subQ9,subQ8,subQ7,subQ6,subQ5,subQ4,subQ3,subQ2,subQ1,subQ0])],"isStart":false})]})])],"isStart":false});}
            var Q4;
            Q4=makeQuery(id+"F8.opExtrude","CAP_EDGE",EDGE,{"disambiguationData":[OSD([sQuery(id+"F0.wireOp",EDGE,"E7.6.0")])],"isStart":false});
            var Q5;
            Q5=makeQuery(id+"F8.opExtrude","CAP_EDGE",EDGE,{"disambiguationData":[OSD([sQuery(id+"F0.wireOp",EDGE,"E7.7.0")])],"isStart":false});
            var Q6;
            Q6=makeQuery(id+"F8.opExtrude","CAP_EDGE",EDGE,{"disambiguationData":[OSD([sQuery(id+"F0.wireOp",EDGE,"E5.0")])],"isStart":false});
            var Q7;
            Q7=makeQuery(id+"F8.opExtrude","CAP_EDGE",EDGE,{"disambiguationData":[OSD([sQuery(id+"F0.wireOp",EDGE,"E7.1.0")])],"isStart":false});
            var Q8;
            {var subQ0=sQuery(id+"F0.wireOp",EDGE,"E7.7.1");var subQ1=sQuery(id+"F0.wireOp",EDGE,"E7.7.0");var subQ2=sQuery(id+"F0.wireOp",EDGE,"E7.6.1");var subQ3=sQuery(id+"F0.wireOp",EDGE,"E7.6.0");var subQ4=sQuery(id+"F0.wireOp",EDGE,"E7.5.1");var subQ5=sQuery(id+"F0.wireOp",EDGE,"E7.5.0");var subQ6=sQuery(id+"F0.wireOp",EDGE,"E7.4.1");var subQ7=sQuery(id+"F0.wireOp",EDGE,"E7.4.0");var subQ8=sQuery(id+"F0.wireOp",EDGE,"E7.3.1");var subQ9=sQuery(id+"F0.wireOp",EDGE,"E7.3.0");var subQ10=sQuery(id+"F0.wireOp",EDGE,"E7.2.1");var subQ11=sQuery(id+"F0.wireOp",EDGE,"E7.2.0");var subQ12=sQuery(id+"F0.wireOp",EDGE,"E7.1.1");var subQ13=sQuery(id+"F0.wireOp",EDGE,"E7.1.0");var subQ14=sQuery(id+"F0.wireOp",EDGE,"E6.0");var subQ15=sQuery(id+"F0.wireOp",EDGE,"E5.0");var subQ16=sQuery(id+"F0.wireOp",EDGE,"E4.0");var subQ17=sQuery(id+"F0.wireOp",EDGE,"E1");var subQ18=sQuery(id+"F0.wireOp",EDGE,"E0");Q8=makeQuery(id+"F8.opExtrude","CAP_EDGE",EDGE,{"disambiguationData":[OSD([subQ18,subQ17,subQ16,subQ15,subQ14,subQ13,subQ12,subQ11,subQ10,subQ9,subQ8,subQ7,subQ6,subQ5,subQ4,subQ3,subQ2,subQ1,subQ0]),TDD([makeQuery(id+"F4.opFillet","BLEND_EDGE",EDGE,{"blendedFrom":[makeQuery(id+"F1.opExtrude","SWEPT_EDGE",EDGE,{"disambiguationData":[OSD([subQ16,subQ10])]}),makeQuery(id+"F1.opExtrude","CAP_FACE",FACE,{"disambiguationData":[OSD([subQ18,subQ17,subQ16,subQ15,subQ14,subQ13,subQ12,subQ11,subQ10,subQ9,subQ8,subQ7,subQ6,subQ5,subQ4,subQ3,subQ2,subQ1,subQ0])],"isStart":false})],"blendedInto":[makeQuery(id+"F1.opExtrude","CAP_FACE",FACE,{"disambiguationData":[OSD([subQ18,subQ17,subQ16,subQ15,subQ14,subQ13,subQ12,subQ11,subQ10,subQ9,subQ8,subQ7,subQ6,subQ5,subQ4,subQ3,subQ2,subQ1,subQ0])],"isStart":false})]})])],"isStart":false});}
            var Q9;
            {var subQ0=sQuery(id+"F0.wireOp",EDGE,"E7.7.1");var subQ1=sQuery(id+"F0.wireOp",EDGE,"E7.7.0");var subQ2=sQuery(id+"F0.wireOp",EDGE,"E7.6.1");var subQ3=sQuery(id+"F0.wireOp",EDGE,"E7.6.0");var subQ4=sQuery(id+"F0.wireOp",EDGE,"E7.5.1");var subQ5=sQuery(id+"F0.wireOp",EDGE,"E7.5.0");var subQ6=sQuery(id+"F0.wireOp",EDGE,"E7.4.1");var subQ7=sQuery(id+"F0.wireOp",EDGE,"E7.4.0");var subQ8=sQuery(id+"F0.wireOp",EDGE,"E7.3.1");var subQ9=sQuery(id+"F0.wireOp",EDGE,"E7.3.0");var subQ10=sQuery(id+"F0.wireOp",EDGE,"E7.2.1");var subQ11=sQuery(id+"F0.wireOp",EDGE,"E7.2.0");var subQ12=sQuery(id+"F0.wireOp",EDGE,"E7.1.1");var subQ13=sQuery(id+"F0.wireOp",EDGE,"E7.1.0");var subQ14=sQuery(id+"F0.wireOp",EDGE,"E6.0");var subQ15=sQuery(id+"F0.wireOp",EDGE,"E5.0");var subQ16=sQuery(id+"F0.wireOp",EDGE,"E4.0");var subQ17=sQuery(id+"F0.wireOp",EDGE,"E1");var subQ18=sQuery(id+"F0.wireOp",EDGE,"E0");Q9=makeQuery(id+"F8.opExtrude","CAP_EDGE",EDGE,{"disambiguationData":[OSD([subQ18,subQ17,subQ16,subQ15,subQ14,subQ13,subQ12,subQ11,subQ10,subQ9,subQ8,subQ7,subQ6,subQ5,subQ4,subQ3,subQ2,subQ1,subQ0]),TDD([makeQuery(id+"F4.opFillet","BLEND_EDGE",EDGE,{"blendedFrom":[makeQuery(id+"F1.opExtrude","SWEPT_EDGE",EDGE,{"disambiguationData":[OSD([subQ16,subQ8])]}),makeQuery(id+"F1.opExtrude","CAP_FACE",FACE,{"disambiguationData":[OSD([subQ18,subQ17,subQ16,subQ15,subQ14,subQ13,subQ12,subQ11,subQ10,subQ9,subQ8,subQ7,subQ6,subQ5,subQ4,subQ3,subQ2,subQ1,subQ0])],"isStart":false})],"blendedInto":[makeQuery(id+"F1.opExtrude","CAP_FACE",FACE,{"disambiguationData":[OSD([subQ18,subQ17,subQ16,subQ15,subQ14,subQ13,subQ12,subQ11,subQ10,subQ9,subQ8,subQ7,subQ6,subQ5,subQ4,subQ3,subQ2,subQ1,subQ0])],"isStart":false})]})])],"isStart":false});}
            var Q10;
            {var subQ0=sQuery(id+"F0.wireOp",EDGE,"E7.7.1");var subQ1=sQuery(id+"F0.wireOp",EDGE,"E7.7.0");var subQ2=sQuery(id+"F0.wireOp",EDGE,"E7.6.1");var subQ3=sQuery(id+"F0.wireOp",EDGE,"E7.6.0");var subQ4=sQuery(id+"F0.wireOp",EDGE,"E7.5.1");var subQ5=sQuery(id+"F0.wireOp",EDGE,"E7.5.0");var subQ6=sQuery(id+"F0.wireOp",EDGE,"E7.4.1");var subQ7=sQuery(id+"F0.wireOp",EDGE,"E7.4.0");var subQ8=sQuery(id+"F0.wireOp",EDGE,"E7.3.1");var subQ9=sQuery(id+"F0.wireOp",EDGE,"E7.3.0");var subQ10=sQuery(id+"F0.wireOp",EDGE,"E7.2.1");var subQ11=sQuery(id+"F0.wireOp",EDGE,"E7.2.0");var subQ12=sQuery(id+"F0.wireOp",EDGE,"E7.1.1");var subQ13=sQuery(id+"F0.wireOp",EDGE,"E7.1.0");var subQ14=sQuery(id+"F0.wireOp",EDGE,"E6.0");var subQ15=sQuery(id+"F0.wireOp",EDGE,"E5.0");var subQ16=sQuery(id+"F0.wireOp",EDGE,"E4.0");var subQ17=sQuery(id+"F0.wireOp",EDGE,"E1");var subQ18=sQuery(id+"F0.wireOp",EDGE,"E0");Q10=makeQuery(id+"F8.opExtrude","CAP_EDGE",EDGE,{"disambiguationData":[OSD([subQ18,subQ17,subQ16,subQ15,subQ14,subQ13,subQ12,subQ11,subQ10,subQ9,subQ8,subQ7,subQ6,subQ5,subQ4,subQ3,subQ2,subQ1,subQ0]),TDD([makeQuery(id+"F4.opFillet","BLEND_EDGE",EDGE,{"blendedFrom":[makeQuery(id+"F1.opExtrude","SWEPT_EDGE",EDGE,{"disambiguationData":[OSD([subQ16,subQ6])]}),makeQuery(id+"F1.opExtrude","CAP_FACE",FACE,{"disambiguationData":[OSD([subQ18,subQ17,subQ16,subQ15,subQ14,subQ13,subQ12,subQ11,subQ10,subQ9,subQ8,subQ7,subQ6,subQ5,subQ4,subQ3,subQ2,subQ1,subQ0])],"isStart":false})],"blendedInto":[makeQuery(id+"F1.opExtrude","CAP_FACE",FACE,{"disambiguationData":[OSD([subQ18,subQ17,subQ16,subQ15,subQ14,subQ13,subQ12,subQ11,subQ10,subQ9,subQ8,subQ7,subQ6,subQ5,subQ4,subQ3,subQ2,subQ1,subQ0])],"isStart":false})]})])],"isStart":false});}
            var Q11;
            Q11=makeQuery(id+"F8.opExtrude","CAP_EDGE",EDGE,{"disambiguationData":[OSD([sQuery(id+"F0.wireOp",EDGE,"E7.3.0")])],"isStart":false});
            var Q12;
            Q12=makeQuery(id+"F8.opExtrude","CAP_EDGE",EDGE,{"disambiguationData":[OSD([sQuery(id+"F0.wireOp",EDGE,"E7.2.0")])],"isStart":false});
            var Q13;
            {var subQ0=sQuery(id+"F0.wireOp",EDGE,"E7.7.1");var subQ1=sQuery(id+"F0.wireOp",EDGE,"E7.7.0");var subQ2=sQuery(id+"F0.wireOp",EDGE,"E7.6.1");var subQ3=sQuery(id+"F0.wireOp",EDGE,"E7.6.0");var subQ4=sQuery(id+"F0.wireOp",EDGE,"E7.5.1");var subQ5=sQuery(id+"F0.wireOp",EDGE,"E7.5.0");var subQ6=sQuery(id+"F0.wireOp",EDGE,"E7.4.1");var subQ7=sQuery(id+"F0.wireOp",EDGE,"E7.4.0");var subQ8=sQuery(id+"F0.wireOp",EDGE,"E7.3.1");var subQ9=sQuery(id+"F0.wireOp",EDGE,"E7.3.0");var subQ10=sQuery(id+"F0.wireOp",EDGE,"E7.2.1");var subQ11=sQuery(id+"F0.wireOp",EDGE,"E7.2.0");var subQ12=sQuery(id+"F0.wireOp",EDGE,"E7.1.1");var subQ13=sQuery(id+"F0.wireOp",EDGE,"E7.1.0");var subQ14=sQuery(id+"F0.wireOp",EDGE,"E6.0");var subQ15=sQuery(id+"F0.wireOp",EDGE,"E5.0");var subQ16=sQuery(id+"F0.wireOp",EDGE,"E4.0");var subQ17=sQuery(id+"F0.wireOp",EDGE,"E1");var subQ18=sQuery(id+"F0.wireOp",EDGE,"E0");Q13=makeQuery(id+"F8.opExtrude","CAP_EDGE",EDGE,{"disambiguationData":[OSD([subQ18,subQ17,subQ16,subQ15,subQ14,subQ13,subQ12,subQ11,subQ10,subQ9,subQ8,subQ7,subQ6,subQ5,subQ4,subQ3,subQ2,subQ1,subQ0]),TDD([makeQuery(id+"F4.opFillet","BLEND_EDGE",EDGE,{"blendedFrom":[makeQuery(id+"F1.opExtrude","SWEPT_EDGE",EDGE,{"disambiguationData":[OSD([subQ16,subQ12])]}),makeQuery(id+"F1.opExtrude","CAP_FACE",FACE,{"disambiguationData":[OSD([subQ18,subQ17,subQ16,subQ15,subQ14,subQ13,subQ12,subQ11,subQ10,subQ9,subQ8,subQ7,subQ6,subQ5,subQ4,subQ3,subQ2,subQ1,subQ0])],"isStart":false})],"blendedInto":[makeQuery(id+"F1.opExtrude","CAP_FACE",FACE,{"disambiguationData":[OSD([subQ18,subQ17,subQ16,subQ15,subQ14,subQ13,subQ12,subQ11,subQ10,subQ9,subQ8,subQ7,subQ6,subQ5,subQ4,subQ3,subQ2,subQ1,subQ0])],"isStart":false})]})])],"isStart":false});}
            var Q14;
            {var subQ0=sQuery(id+"F0.wireOp",EDGE,"E7.7.1");var subQ1=sQuery(id+"F0.wireOp",EDGE,"E7.7.0");var subQ2=sQuery(id+"F0.wireOp",EDGE,"E7.6.1");var subQ3=sQuery(id+"F0.wireOp",EDGE,"E7.6.0");var subQ4=sQuery(id+"F0.wireOp",EDGE,"E7.5.1");var subQ5=sQuery(id+"F0.wireOp",EDGE,"E7.5.0");var subQ6=sQuery(id+"F0.wireOp",EDGE,"E7.4.1");var subQ7=sQuery(id+"F0.wireOp",EDGE,"E7.4.0");var subQ8=sQuery(id+"F0.wireOp",EDGE,"E7.3.1");var subQ9=sQuery(id+"F0.wireOp",EDGE,"E7.3.0");var subQ10=sQuery(id+"F0.wireOp",EDGE,"E7.2.1");var subQ11=sQuery(id+"F0.wireOp",EDGE,"E7.2.0");var subQ12=sQuery(id+"F0.wireOp",EDGE,"E7.1.1");var subQ13=sQuery(id+"F0.wireOp",EDGE,"E7.1.0");var subQ14=sQuery(id+"F0.wireOp",EDGE,"E6.0");var subQ15=sQuery(id+"F0.wireOp",EDGE,"E5.0");var subQ16=sQuery(id+"F0.wireOp",EDGE,"E4.0");var subQ17=sQuery(id+"F0.wireOp",EDGE,"E1");var subQ18=sQuery(id+"F0.wireOp",EDGE,"E0");Q14=makeQuery(id+"F8.opExtrude","CAP_EDGE",EDGE,{"disambiguationData":[OSD([subQ18,subQ17,subQ16,subQ15,subQ14,subQ13,subQ12,subQ11,subQ10,subQ9,subQ8,subQ7,subQ6,subQ5,subQ4,subQ3,subQ2,subQ1,subQ0]),TDD([makeQuery(id+"F4.opFillet","BLEND_EDGE",EDGE,{"blendedFrom":[makeQuery(id+"F1.opExtrude","SWEPT_EDGE",EDGE,{"disambiguationData":[OSD([subQ16,subQ14])]}),makeQuery(id+"F1.opExtrude","CAP_FACE",FACE,{"disambiguationData":[OSD([subQ18,subQ17,subQ16,subQ15,subQ14,subQ13,subQ12,subQ11,subQ10,subQ9,subQ8,subQ7,subQ6,subQ5,subQ4,subQ3,subQ2,subQ1,subQ0])],"isStart":false})],"blendedInto":[makeQuery(id+"F1.opExtrude","CAP_FACE",FACE,{"disambiguationData":[OSD([subQ18,subQ17,subQ16,subQ15,subQ14,subQ13,subQ12,subQ11,subQ10,subQ9,subQ8,subQ7,subQ6,subQ5,subQ4,subQ3,subQ2,subQ1,subQ0])],"isStart":false})]})])],"isStart":false});}
            var Q15;
            {var subQ0=sQuery(id+"F0.wireOp",EDGE,"E7.7.1");var subQ1=sQuery(id+"F0.wireOp",EDGE,"E7.7.0");var subQ2=sQuery(id+"F0.wireOp",EDGE,"E7.6.1");var subQ3=sQuery(id+"F0.wireOp",EDGE,"E7.6.0");var subQ4=sQuery(id+"F0.wireOp",EDGE,"E7.5.1");var subQ5=sQuery(id+"F0.wireOp",EDGE,"E7.5.0");var subQ6=sQuery(id+"F0.wireOp",EDGE,"E7.4.1");var subQ7=sQuery(id+"F0.wireOp",EDGE,"E7.4.0");var subQ8=sQuery(id+"F0.wireOp",EDGE,"E7.3.1");var subQ9=sQuery(id+"F0.wireOp",EDGE,"E7.3.0");var subQ10=sQuery(id+"F0.wireOp",EDGE,"E7.2.1");var subQ11=sQuery(id+"F0.wireOp",EDGE,"E7.2.0");var subQ12=sQuery(id+"F0.wireOp",EDGE,"E7.1.1");var subQ13=sQuery(id+"F0.wireOp",EDGE,"E7.1.0");var subQ14=sQuery(id+"F0.wireOp",EDGE,"E6.0");var subQ15=sQuery(id+"F0.wireOp",EDGE,"E5.0");var subQ16=sQuery(id+"F0.wireOp",EDGE,"E4.0");var subQ17=sQuery(id+"F0.wireOp",EDGE,"E1");var subQ18=sQuery(id+"F0.wireOp",EDGE,"E0");Q15=makeQuery(id+"F8.opExtrude","CAP_EDGE",EDGE,{"disambiguationData":[OSD([subQ18,subQ17,subQ16,subQ15,subQ14,subQ13,subQ12,subQ11,subQ10,subQ9,subQ8,subQ7,subQ6,subQ5,subQ4,subQ3,subQ2,subQ1,subQ0]),TDD([makeQuery(id+"F4.opFillet","BLEND_EDGE",EDGE,{"blendedFrom":[makeQuery(id+"F1.opExtrude","SWEPT_EDGE",EDGE,{"disambiguationData":[OSD([subQ16,subQ0])]}),makeQuery(id+"F1.opExtrude","CAP_FACE",FACE,{"disambiguationData":[OSD([subQ18,subQ17,subQ16,subQ15,subQ14,subQ13,subQ12,subQ11,subQ10,subQ9,subQ8,subQ7,subQ6,subQ5,subQ4,subQ3,subQ2,subQ1,subQ0])],"isStart":false})],"blendedInto":[makeQuery(id+"F1.opExtrude","CAP_FACE",FACE,{"disambiguationData":[OSD([subQ18,subQ17,subQ16,subQ15,subQ14,subQ13,subQ12,subQ11,subQ10,subQ9,subQ8,subQ7,subQ6,subQ5,subQ4,subQ3,subQ2,subQ1,subQ0])],"isStart":false})]})])],"isStart":false});}
            chamfer(context, id + "F9", {"entities" : qUnion([Q0, Q1, Q2, Q3, Q4, Q5, Q6, Q7, Q8, Q9, Q10, Q11, Q12, Q13, Q14, Q15]), "chamferType" : ChamferType.TWO_OFFSETS, "width1" : 4 * mm, "oppositeDirection" : false, "width2" : 3.3 * mm, "tangentPropagation" : true});
        }
        {
            var Q0;
            {var subQ0=sQuery(id+"F0.wireOp",EDGE,"E7.7.1");var subQ1=sQuery(id+"F0.wireOp",EDGE,"E7.7.0");var subQ2=sQuery(id+"F0.wireOp",EDGE,"E7.6.1");var subQ3=sQuery(id+"F0.wireOp",EDGE,"E7.6.0");var subQ4=sQuery(id+"F0.wireOp",EDGE,"E7.5.1");var subQ5=sQuery(id+"F0.wireOp",EDGE,"E7.5.0");var subQ6=sQuery(id+"F0.wireOp",EDGE,"E7.4.1");var subQ7=sQuery(id+"F0.wireOp",EDGE,"E7.4.0");var subQ8=sQuery(id+"F0.wireOp",EDGE,"E7.3.1");var subQ9=sQuery(id+"F0.wireOp",EDGE,"E7.3.0");var subQ10=sQuery(id+"F0.wireOp",EDGE,"E7.2.1");var subQ11=sQuery(id+"F0.wireOp",EDGE,"E7.2.0");var subQ12=sQuery(id+"F0.wireOp",EDGE,"E7.1.1");var subQ13=sQuery(id+"F0.wireOp",EDGE,"E7.1.0");var subQ14=sQuery(id+"F0.wireOp",EDGE,"E6.0");var subQ15=sQuery(id+"F0.wireOp",EDGE,"E5.0");var subQ16=sQuery(id+"F0.wireOp",EDGE,"E4.0");var subQ17=sQuery(id+"F0.wireOp",EDGE,"E1");var subQ18=sQuery(id+"F0.wireOp",EDGE,"E0");var subQ19=makeQuery(id+"F4.opFillet","BLEND_EDGE",EDGE,{"blendedFrom":[makeQuery(id+"F1.opExtrude","SWEPT_EDGE",EDGE,{"disambiguationData":[OSD([subQ16,subQ0])]}),makeQuery(id+"F1.opExtrude","CAP_FACE",FACE,{"disambiguationData":[OSD([subQ18,subQ17,subQ16,subQ15,subQ14,subQ13,subQ12,subQ11,subQ10,subQ9,subQ8,subQ7,subQ6,subQ5,subQ4,subQ3,subQ2,subQ1,subQ0])],"isStart":false})],"blendedInto":[makeQuery(id+"F1.opExtrude","CAP_FACE",FACE,{"disambiguationData":[OSD([subQ18,subQ17,subQ16,subQ15,subQ14,subQ13,subQ12,subQ11,subQ10,subQ9,subQ8,subQ7,subQ6,subQ5,subQ4,subQ3,subQ2,subQ1,subQ0])],"isStart":false})]});Q0=makeQuery(id+"F9.opChamfer","BLEND_EDGE",EDGE,{"blendedFrom":[makeQuery(id+"F8.opExtrude","CAP_EDGE",EDGE,{"disambiguationData":[OSD([subQ18,subQ17,subQ16,subQ15,subQ14,subQ13,subQ12,subQ11,subQ10,subQ9,subQ8,subQ7,subQ6,subQ5,subQ4,subQ3,subQ2,subQ1,subQ0]),TDD([subQ19])],"isStart":false}),makeQuery(id+"F8.boolean.opBoolean","MERGE",FACE,{"derivedFrom":[makeQuery(id+"F4.opFillet","BLEND_FACE",FACE,{"disambiguationData":[OSD([subQ16,subQ0])]}),makeQuery(id+"F8.opExtrude","SWEPT_FACE",FACE,{"disambiguationData":[OSD([subQ18,subQ17,subQ16,subQ15,subQ14,subQ13,subQ12,subQ11,subQ10,subQ9,subQ8,subQ7,subQ6,subQ5,subQ4,subQ3,subQ2,subQ1,subQ0]),TDD([subQ19])]})]})],"blendedInto":[makeQuery(id+"F8.boolean.opBoolean","MERGE",FACE,{"derivedFrom":[makeQuery(id+"F4.opFillet","BLEND_FACE",FACE,{"disambiguationData":[OSD([subQ16,subQ0])]}),makeQuery(id+"F8.opExtrude","SWEPT_FACE",FACE,{"disambiguationData":[OSD([subQ18,subQ17,subQ16,subQ15,subQ14,subQ13,subQ12,subQ11,subQ10,subQ9,subQ8,subQ7,subQ6,subQ5,subQ4,subQ3,subQ2,subQ1,subQ0]),TDD([subQ19])]})]})]});}
            var Q1;
            {var subQ0=sQuery(id+"F0.wireOp",EDGE,"E7.7.1");var subQ1=sQuery(id+"F0.wireOp",EDGE,"E7.7.0");var subQ2=sQuery(id+"F0.wireOp",EDGE,"E7.6.1");var subQ3=sQuery(id+"F0.wireOp",EDGE,"E7.6.0");var subQ4=sQuery(id+"F0.wireOp",EDGE,"E7.5.1");var subQ5=sQuery(id+"F0.wireOp",EDGE,"E7.5.0");var subQ6=sQuery(id+"F0.wireOp",EDGE,"E7.4.1");var subQ7=sQuery(id+"F0.wireOp",EDGE,"E7.4.0");var subQ8=sQuery(id+"F0.wireOp",EDGE,"E7.3.1");var subQ9=sQuery(id+"F0.wireOp",EDGE,"E7.3.0");var subQ10=sQuery(id+"F0.wireOp",EDGE,"E7.2.1");var subQ11=sQuery(id+"F0.wireOp",EDGE,"E7.2.0");var subQ12=sQuery(id+"F0.wireOp",EDGE,"E7.1.1");var subQ13=sQuery(id+"F0.wireOp",EDGE,"E7.1.0");var subQ14=sQuery(id+"F0.wireOp",EDGE,"E6.0");var subQ15=sQuery(id+"F0.wireOp",EDGE,"E5.0");var subQ16=sQuery(id+"F0.wireOp",EDGE,"E4.0");var subQ17=sQuery(id+"F0.wireOp",EDGE,"E1");var subQ18=sQuery(id+"F0.wireOp",EDGE,"E0");var subQ19=makeQuery(id+"F3.opFillet","BLEND_EDGE",EDGE,{"blendedFrom":[makeQuery(id+"F1.opExtrude","SWEPT_EDGE",EDGE,{"disambiguationData":[OSD([subQ16,subQ1])]}),makeQuery(id+"F1.opExtrude","CAP_FACE",FACE,{"disambiguationData":[OSD([subQ18,subQ17,subQ16,subQ15,subQ14,subQ13,subQ12,subQ11,subQ10,subQ9,subQ8,subQ7,subQ6,subQ5,subQ4,subQ3,subQ2,subQ1,subQ0])],"isStart":false})],"blendedInto":[makeQuery(id+"F1.opExtrude","CAP_FACE",FACE,{"disambiguationData":[OSD([subQ18,subQ17,subQ16,subQ15,subQ14,subQ13,subQ12,subQ11,subQ10,subQ9,subQ8,subQ7,subQ6,subQ5,subQ4,subQ3,subQ2,subQ1,subQ0])],"isStart":false})]});Q1=makeQuery(id+"F9.opChamfer","BLEND_EDGE",EDGE,{"blendedFrom":[makeQuery(id+"F8.opExtrude","CAP_EDGE",EDGE,{"disambiguationData":[OSD([subQ18,subQ17,subQ16,subQ15,subQ14,subQ13,subQ12,subQ11,subQ10,subQ9,subQ8,subQ7,subQ6,subQ5,subQ4,subQ3,subQ2,subQ1,subQ0]),TDD([subQ19])],"isStart":false}),makeQuery(id+"F8.boolean.opBoolean","MERGE",FACE,{"derivedFrom":[makeQuery(id+"F3.opFillet","BLEND_FACE",FACE,{"disambiguationData":[OSD([subQ16,subQ1])]}),makeQuery(id+"F8.opExtrude","SWEPT_FACE",FACE,{"disambiguationData":[OSD([subQ18,subQ17,subQ16,subQ15,subQ14,subQ13,subQ12,subQ11,subQ10,subQ9,subQ8,subQ7,subQ6,subQ5,subQ4,subQ3,subQ2,subQ1,subQ0]),TDD([subQ19])]})]})],"blendedInto":[makeQuery(id+"F8.boolean.opBoolean","MERGE",FACE,{"derivedFrom":[makeQuery(id+"F3.opFillet","BLEND_FACE",FACE,{"disambiguationData":[OSD([subQ16,subQ1])]}),makeQuery(id+"F8.opExtrude","SWEPT_FACE",FACE,{"disambiguationData":[OSD([subQ18,subQ17,subQ16,subQ15,subQ14,subQ13,subQ12,subQ11,subQ10,subQ9,subQ8,subQ7,subQ6,subQ5,subQ4,subQ3,subQ2,subQ1,subQ0]),TDD([subQ19])]})]})]});}
            var Q2;
            {var subQ0=sQuery(id+"F0.wireOp",EDGE,"E5.0");Q2=makeQuery(id+"F9.opChamfer","BLEND_EDGE",EDGE,{"blendedFrom":[makeQuery(id+"F8.opExtrude","CAP_EDGE",EDGE,{"disambiguationData":[OSD([subQ0])],"isStart":false}),makeQuery(id+"F8.boolean.opBoolean","MERGE",FACE,{"derivedFrom":[makeQuery(id+"F1.opExtrude","SWEPT_FACE",FACE,{"disambiguationData":[OSD([subQ0])]}),makeQuery(id+"F8.opExtrude","SWEPT_FACE",FACE,{"disambiguationData":[OSD([subQ0])]})]})],"blendedInto":[makeQuery(id+"F8.boolean.opBoolean","MERGE",FACE,{"derivedFrom":[makeQuery(id+"F1.opExtrude","SWEPT_FACE",FACE,{"disambiguationData":[OSD([subQ0])]}),makeQuery(id+"F8.opExtrude","SWEPT_FACE",FACE,{"disambiguationData":[OSD([subQ0])]})]})]});}
            var Q3;
            {var subQ0=sQuery(id+"F0.wireOp",EDGE,"E7.1.0");Q3=makeQuery(id+"F9.opChamfer","BLEND_EDGE",EDGE,{"blendedFrom":[makeQuery(id+"F8.opExtrude","CAP_EDGE",EDGE,{"disambiguationData":[OSD([subQ0])],"isStart":false}),makeQuery(id+"F8.boolean.opBoolean","MERGE",FACE,{"derivedFrom":[makeQuery(id+"F1.opExtrude","SWEPT_FACE",FACE,{"disambiguationData":[OSD([subQ0])]}),makeQuery(id+"F8.opExtrude","SWEPT_FACE",FACE,{"disambiguationData":[OSD([subQ0])]})]})],"blendedInto":[makeQuery(id+"F8.boolean.opBoolean","MERGE",FACE,{"derivedFrom":[makeQuery(id+"F1.opExtrude","SWEPT_FACE",FACE,{"disambiguationData":[OSD([subQ0])]}),makeQuery(id+"F8.opExtrude","SWEPT_FACE",FACE,{"disambiguationData":[OSD([subQ0])]})]})]});}
            var Q4;
            {var subQ0=sQuery(id+"F0.wireOp",EDGE,"E7.7.1");var subQ1=sQuery(id+"F0.wireOp",EDGE,"E7.7.0");var subQ2=sQuery(id+"F0.wireOp",EDGE,"E7.6.1");var subQ3=sQuery(id+"F0.wireOp",EDGE,"E7.6.0");var subQ4=sQuery(id+"F0.wireOp",EDGE,"E7.5.1");var subQ5=sQuery(id+"F0.wireOp",EDGE,"E7.5.0");var subQ6=sQuery(id+"F0.wireOp",EDGE,"E7.4.1");var subQ7=sQuery(id+"F0.wireOp",EDGE,"E7.4.0");var subQ8=sQuery(id+"F0.wireOp",EDGE,"E7.3.1");var subQ9=sQuery(id+"F0.wireOp",EDGE,"E7.3.0");var subQ10=sQuery(id+"F0.wireOp",EDGE,"E7.2.1");var subQ11=sQuery(id+"F0.wireOp",EDGE,"E7.2.0");var subQ12=sQuery(id+"F0.wireOp",EDGE,"E7.1.1");var subQ13=sQuery(id+"F0.wireOp",EDGE,"E7.1.0");var subQ14=sQuery(id+"F0.wireOp",EDGE,"E6.0");var subQ15=sQuery(id+"F0.wireOp",EDGE,"E5.0");var subQ16=sQuery(id+"F0.wireOp",EDGE,"E4.0");var subQ17=sQuery(id+"F0.wireOp",EDGE,"E1");var subQ18=sQuery(id+"F0.wireOp",EDGE,"E0");var subQ19=makeQuery(id+"F4.opFillet","BLEND_EDGE",EDGE,{"blendedFrom":[makeQuery(id+"F1.opExtrude","SWEPT_EDGE",EDGE,{"disambiguationData":[OSD([subQ16,subQ8])]}),makeQuery(id+"F1.opExtrude","CAP_FACE",FACE,{"disambiguationData":[OSD([subQ18,subQ17,subQ16,subQ15,subQ14,subQ13,subQ12,subQ11,subQ10,subQ9,subQ8,subQ7,subQ6,subQ5,subQ4,subQ3,subQ2,subQ1,subQ0])],"isStart":false})],"blendedInto":[makeQuery(id+"F1.opExtrude","CAP_FACE",FACE,{"disambiguationData":[OSD([subQ18,subQ17,subQ16,subQ15,subQ14,subQ13,subQ12,subQ11,subQ10,subQ9,subQ8,subQ7,subQ6,subQ5,subQ4,subQ3,subQ2,subQ1,subQ0])],"isStart":false})]});Q4=makeQuery(id+"F9.opChamfer","BLEND_EDGE",EDGE,{"blendedFrom":[makeQuery(id+"F8.opExtrude","CAP_EDGE",EDGE,{"disambiguationData":[OSD([subQ18,subQ17,subQ16,subQ15,subQ14,subQ13,subQ12,subQ11,subQ10,subQ9,subQ8,subQ7,subQ6,subQ5,subQ4,subQ3,subQ2,subQ1,subQ0]),TDD([subQ19])],"isStart":false}),makeQuery(id+"F8.boolean.opBoolean","MERGE",FACE,{"derivedFrom":[makeQuery(id+"F4.opFillet","BLEND_FACE",FACE,{"disambiguationData":[OSD([subQ16,subQ8])]}),makeQuery(id+"F8.opExtrude","SWEPT_FACE",FACE,{"disambiguationData":[OSD([subQ18,subQ17,subQ16,subQ15,subQ14,subQ13,subQ12,subQ11,subQ10,subQ9,subQ8,subQ7,subQ6,subQ5,subQ4,subQ3,subQ2,subQ1,subQ0]),TDD([subQ19])]})]})],"blendedInto":[makeQuery(id+"F8.boolean.opBoolean","MERGE",FACE,{"derivedFrom":[makeQuery(id+"F4.opFillet","BLEND_FACE",FACE,{"disambiguationData":[OSD([subQ16,subQ8])]}),makeQuery(id+"F8.opExtrude","SWEPT_FACE",FACE,{"disambiguationData":[OSD([subQ18,subQ17,subQ16,subQ15,subQ14,subQ13,subQ12,subQ11,subQ10,subQ9,subQ8,subQ7,subQ6,subQ5,subQ4,subQ3,subQ2,subQ1,subQ0]),TDD([subQ19])]})]})]});}
            var Q5;
            {var subQ0=sQuery(id+"F0.wireOp",EDGE,"E7.7.1");var subQ1=sQuery(id+"F0.wireOp",EDGE,"E7.7.0");var subQ2=sQuery(id+"F0.wireOp",EDGE,"E7.6.1");var subQ3=sQuery(id+"F0.wireOp",EDGE,"E7.6.0");var subQ4=sQuery(id+"F0.wireOp",EDGE,"E7.5.1");var subQ5=sQuery(id+"F0.wireOp",EDGE,"E7.5.0");var subQ6=sQuery(id+"F0.wireOp",EDGE,"E7.4.1");var subQ7=sQuery(id+"F0.wireOp",EDGE,"E7.4.0");var subQ8=sQuery(id+"F0.wireOp",EDGE,"E7.3.1");var subQ9=sQuery(id+"F0.wireOp",EDGE,"E7.3.0");var subQ10=sQuery(id+"F0.wireOp",EDGE,"E7.2.1");var subQ11=sQuery(id+"F0.wireOp",EDGE,"E7.2.0");var subQ12=sQuery(id+"F0.wireOp",EDGE,"E7.1.1");var subQ13=sQuery(id+"F0.wireOp",EDGE,"E7.1.0");var subQ14=sQuery(id+"F0.wireOp",EDGE,"E6.0");var subQ15=sQuery(id+"F0.wireOp",EDGE,"E5.0");var subQ16=sQuery(id+"F0.wireOp",EDGE,"E4.0");var subQ17=sQuery(id+"F0.wireOp",EDGE,"E1");var subQ18=sQuery(id+"F0.wireOp",EDGE,"E0");var subQ19=makeQuery(id+"F4.opFillet","BLEND_EDGE",EDGE,{"blendedFrom":[makeQuery(id+"F1.opExtrude","SWEPT_EDGE",EDGE,{"disambiguationData":[OSD([subQ16,subQ6])]}),makeQuery(id+"F1.opExtrude","CAP_FACE",FACE,{"disambiguationData":[OSD([subQ18,subQ17,subQ16,subQ15,subQ14,subQ13,subQ12,subQ11,subQ10,subQ9,subQ8,subQ7,subQ6,subQ5,subQ4,subQ3,subQ2,subQ1,subQ0])],"isStart":false})],"blendedInto":[makeQuery(id+"F1.opExtrude","CAP_FACE",FACE,{"disambiguationData":[OSD([subQ18,subQ17,subQ16,subQ15,subQ14,subQ13,subQ12,subQ11,subQ10,subQ9,subQ8,subQ7,subQ6,subQ5,subQ4,subQ3,subQ2,subQ1,subQ0])],"isStart":false})]});Q5=makeQuery(id+"F9.opChamfer","BLEND_EDGE",EDGE,{"blendedFrom":[makeQuery(id+"F8.opExtrude","CAP_EDGE",EDGE,{"disambiguationData":[OSD([subQ18,subQ17,subQ16,subQ15,subQ14,subQ13,subQ12,subQ11,subQ10,subQ9,subQ8,subQ7,subQ6,subQ5,subQ4,subQ3,subQ2,subQ1,subQ0]),TDD([subQ19])],"isStart":false}),makeQuery(id+"F8.boolean.opBoolean","MERGE",FACE,{"derivedFrom":[makeQuery(id+"F4.opFillet","BLEND_FACE",FACE,{"disambiguationData":[OSD([subQ16,subQ6])]}),makeQuery(id+"F8.opExtrude","SWEPT_FACE",FACE,{"disambiguationData":[OSD([subQ18,subQ17,subQ16,subQ15,subQ14,subQ13,subQ12,subQ11,subQ10,subQ9,subQ8,subQ7,subQ6,subQ5,subQ4,subQ3,subQ2,subQ1,subQ0]),TDD([subQ19])]})]})],"blendedInto":[makeQuery(id+"F8.boolean.opBoolean","MERGE",FACE,{"derivedFrom":[makeQuery(id+"F4.opFillet","BLEND_FACE",FACE,{"disambiguationData":[OSD([subQ16,subQ6])]}),makeQuery(id+"F8.opExtrude","SWEPT_FACE",FACE,{"disambiguationData":[OSD([subQ18,subQ17,subQ16,subQ15,subQ14,subQ13,subQ12,subQ11,subQ10,subQ9,subQ8,subQ7,subQ6,subQ5,subQ4,subQ3,subQ2,subQ1,subQ0]),TDD([subQ19])]})]})]});}
            var Q6;
            {var subQ0=sQuery(id+"F0.wireOp",EDGE,"E7.7.1");var subQ1=sQuery(id+"F0.wireOp",EDGE,"E7.7.0");var subQ2=sQuery(id+"F0.wireOp",EDGE,"E7.6.1");var subQ3=sQuery(id+"F0.wireOp",EDGE,"E7.6.0");var subQ4=sQuery(id+"F0.wireOp",EDGE,"E7.5.1");var subQ5=sQuery(id+"F0.wireOp",EDGE,"E7.5.0");var subQ6=sQuery(id+"F0.wireOp",EDGE,"E7.4.1");var subQ7=sQuery(id+"F0.wireOp",EDGE,"E7.4.0");var subQ8=sQuery(id+"F0.wireOp",EDGE,"E7.3.1");var subQ9=sQuery(id+"F0.wireOp",EDGE,"E7.3.0");var subQ10=sQuery(id+"F0.wireOp",EDGE,"E7.2.1");var subQ11=sQuery(id+"F0.wireOp",EDGE,"E7.2.0");var subQ12=sQuery(id+"F0.wireOp",EDGE,"E7.1.1");var subQ13=sQuery(id+"F0.wireOp",EDGE,"E7.1.0");var subQ14=sQuery(id+"F0.wireOp",EDGE,"E6.0");var subQ15=sQuery(id+"F0.wireOp",EDGE,"E5.0");var subQ16=sQuery(id+"F0.wireOp",EDGE,"E4.0");var subQ17=sQuery(id+"F0.wireOp",EDGE,"E1");var subQ18=sQuery(id+"F0.wireOp",EDGE,"E0");var subQ19=makeQuery(id+"F4.opFillet","BLEND_EDGE",EDGE,{"blendedFrom":[makeQuery(id+"F1.opExtrude","SWEPT_EDGE",EDGE,{"disambiguationData":[OSD([subQ16,subQ4])]}),makeQuery(id+"F1.opExtrude","CAP_FACE",FACE,{"disambiguationData":[OSD([subQ18,subQ17,subQ16,subQ15,subQ14,subQ13,subQ12,subQ11,subQ10,subQ9,subQ8,subQ7,subQ6,subQ5,subQ4,subQ3,subQ2,subQ1,subQ0])],"isStart":false})],"blendedInto":[makeQuery(id+"F1.opExtrude","CAP_FACE",FACE,{"disambiguationData":[OSD([subQ18,subQ17,subQ16,subQ15,subQ14,subQ13,subQ12,subQ11,subQ10,subQ9,subQ8,subQ7,subQ6,subQ5,subQ4,subQ3,subQ2,subQ1,subQ0])],"isStart":false})]});Q6=makeQuery(id+"F9.opChamfer","BLEND_EDGE",EDGE,{"blendedFrom":[makeQuery(id+"F8.opExtrude","CAP_EDGE",EDGE,{"disambiguationData":[OSD([subQ18,subQ17,subQ16,subQ15,subQ14,subQ13,subQ12,subQ11,subQ10,subQ9,subQ8,subQ7,subQ6,subQ5,subQ4,subQ3,subQ2,subQ1,subQ0]),TDD([subQ19])],"isStart":false}),makeQuery(id+"F8.boolean.opBoolean","MERGE",FACE,{"derivedFrom":[makeQuery(id+"F4.opFillet","BLEND_FACE",FACE,{"disambiguationData":[OSD([subQ16,subQ4])]}),makeQuery(id+"F8.opExtrude","SWEPT_FACE",FACE,{"disambiguationData":[OSD([subQ18,subQ17,subQ16,subQ15,subQ14,subQ13,subQ12,subQ11,subQ10,subQ9,subQ8,subQ7,subQ6,subQ5,subQ4,subQ3,subQ2,subQ1,subQ0]),TDD([subQ19])]})]})],"blendedInto":[makeQuery(id+"F8.boolean.opBoolean","MERGE",FACE,{"derivedFrom":[makeQuery(id+"F4.opFillet","BLEND_FACE",FACE,{"disambiguationData":[OSD([subQ16,subQ4])]}),makeQuery(id+"F8.opExtrude","SWEPT_FACE",FACE,{"disambiguationData":[OSD([subQ18,subQ17,subQ16,subQ15,subQ14,subQ13,subQ12,subQ11,subQ10,subQ9,subQ8,subQ7,subQ6,subQ5,subQ4,subQ3,subQ2,subQ1,subQ0]),TDD([subQ19])]})]})]});}
            var Q7;
            {var subQ0=sQuery(id+"F0.wireOp",EDGE,"E7.7.1");var subQ1=sQuery(id+"F0.wireOp",EDGE,"E7.7.0");var subQ2=sQuery(id+"F0.wireOp",EDGE,"E7.6.1");var subQ3=sQuery(id+"F0.wireOp",EDGE,"E7.6.0");var subQ4=sQuery(id+"F0.wireOp",EDGE,"E7.5.1");var subQ5=sQuery(id+"F0.wireOp",EDGE,"E7.5.0");var subQ6=sQuery(id+"F0.wireOp",EDGE,"E7.4.1");var subQ7=sQuery(id+"F0.wireOp",EDGE,"E7.4.0");var subQ8=sQuery(id+"F0.wireOp",EDGE,"E7.3.1");var subQ9=sQuery(id+"F0.wireOp",EDGE,"E7.3.0");var subQ10=sQuery(id+"F0.wireOp",EDGE,"E7.2.1");var subQ11=sQuery(id+"F0.wireOp",EDGE,"E7.2.0");var subQ12=sQuery(id+"F0.wireOp",EDGE,"E7.1.1");var subQ13=sQuery(id+"F0.wireOp",EDGE,"E7.1.0");var subQ14=sQuery(id+"F0.wireOp",EDGE,"E6.0");var subQ15=sQuery(id+"F0.wireOp",EDGE,"E5.0");var subQ16=sQuery(id+"F0.wireOp",EDGE,"E4.0");var subQ17=sQuery(id+"F0.wireOp",EDGE,"E1");var subQ18=sQuery(id+"F0.wireOp",EDGE,"E0");var subQ19=makeQuery(id+"F4.opFillet","BLEND_EDGE",EDGE,{"blendedFrom":[makeQuery(id+"F1.opExtrude","SWEPT_EDGE",EDGE,{"disambiguationData":[OSD([subQ16,subQ2])]}),makeQuery(id+"F1.opExtrude","CAP_FACE",FACE,{"disambiguationData":[OSD([subQ18,subQ17,subQ16,subQ15,subQ14,subQ13,subQ12,subQ11,subQ10,subQ9,subQ8,subQ7,subQ6,subQ5,subQ4,subQ3,subQ2,subQ1,subQ0])],"isStart":false})],"blendedInto":[makeQuery(id+"F1.opExtrude","CAP_FACE",FACE,{"disambiguationData":[OSD([subQ18,subQ17,subQ16,subQ15,subQ14,subQ13,subQ12,subQ11,subQ10,subQ9,subQ8,subQ7,subQ6,subQ5,subQ4,subQ3,subQ2,subQ1,subQ0])],"isStart":false})]});Q7=makeQuery(id+"F9.opChamfer","BLEND_EDGE",EDGE,{"blendedFrom":[makeQuery(id+"F8.opExtrude","CAP_EDGE",EDGE,{"disambiguationData":[OSD([subQ18,subQ17,subQ16,subQ15,subQ14,subQ13,subQ12,subQ11,subQ10,subQ9,subQ8,subQ7,subQ6,subQ5,subQ4,subQ3,subQ2,subQ1,subQ0]),TDD([subQ19])],"isStart":false}),makeQuery(id+"F8.boolean.opBoolean","MERGE",FACE,{"derivedFrom":[makeQuery(id+"F4.opFillet","BLEND_FACE",FACE,{"disambiguationData":[OSD([subQ16,subQ2])]}),makeQuery(id+"F8.opExtrude","SWEPT_FACE",FACE,{"disambiguationData":[OSD([subQ18,subQ17,subQ16,subQ15,subQ14,subQ13,subQ12,subQ11,subQ10,subQ9,subQ8,subQ7,subQ6,subQ5,subQ4,subQ3,subQ2,subQ1,subQ0]),TDD([subQ19])]})]})],"blendedInto":[makeQuery(id+"F8.boolean.opBoolean","MERGE",FACE,{"derivedFrom":[makeQuery(id+"F4.opFillet","BLEND_FACE",FACE,{"disambiguationData":[OSD([subQ16,subQ2])]}),makeQuery(id+"F8.opExtrude","SWEPT_FACE",FACE,{"disambiguationData":[OSD([subQ18,subQ17,subQ16,subQ15,subQ14,subQ13,subQ12,subQ11,subQ10,subQ9,subQ8,subQ7,subQ6,subQ5,subQ4,subQ3,subQ2,subQ1,subQ0]),TDD([subQ19])]})]})]});}
            fillet(context, id + "F10", {"entities" : qUnion([Q0, Q1, Q2, Q3, Q4, Q5, Q6, Q7]), "radius" : 7 * mm, "tangentPropagation" : true, "allowEdgeOverflow" : false});
        }
        {
            var Q0;
            Q0=makeQuery(id+"F1.opExtrude","SWEPT_BODY",BODY,{"disambiguationData":[OSD([sQuery(id+"F0.wireOp",EDGE,"E0"),sQuery(id+"F0.wireOp",EDGE,"E1"),sQuery(id+"F0.wireOp",EDGE,"E4.0"),sQuery(id+"F0.wireOp",EDGE,"E5.0"),sQuery(id+"F0.wireOp",EDGE,"E6.0"),sQuery(id+"F0.wireOp",EDGE,"E7.1.0"),sQuery(id+"F0.wireOp",EDGE,"E7.1.1"),sQuery(id+"F0.wireOp",EDGE,"E7.2.0"),sQuery(id+"F0.wireOp",EDGE,"E7.2.1"),sQuery(id+"F0.wireOp",EDGE,"E7.3.0"),sQuery(id+"F0.wireOp",EDGE,"E7.3.1"),sQuery(id+"F0.wireOp",EDGE,"E7.4.0"),sQuery(id+"F0.wireOp",EDGE,"E7.4.1"),sQuery(id+"F0.wireOp",EDGE,"E7.5.0"),sQuery(id+"F0.wireOp",EDGE,"E7.5.1"),sQuery(id+"F0.wireOp",EDGE,"E7.6.0"),sQuery(id+"F0.wireOp",EDGE,"E7.6.1"),sQuery(id+"F0.wireOp",EDGE,"E7.7.0"),sQuery(id+"F0.wireOp",EDGE,"E7.7.1")])]});
            var Q1;
            Q1=makeQuery(id+"F1.opExtrude","CAP_FACE",FACE,{"disambiguationData":[OSD([sQuery(id+"F0.wireOp",EDGE,"E0"),sQuery(id+"F0.wireOp",EDGE,"E1"),sQuery(id+"F0.wireOp",EDGE,"E4.0"),sQuery(id+"F0.wireOp",EDGE,"E5.0"),sQuery(id+"F0.wireOp",EDGE,"E6.0"),sQuery(id+"F0.wireOp",EDGE,"E7.1.0"),sQuery(id+"F0.wireOp",EDGE,"E7.1.1"),sQuery(id+"F0.wireOp",EDGE,"E7.2.0"),sQuery(id+"F0.wireOp",EDGE,"E7.2.1"),sQuery(id+"F0.wireOp",EDGE,"E7.3.0"),sQuery(id+"F0.wireOp",EDGE,"E7.3.1"),sQuery(id+"F0.wireOp",EDGE,"E7.4.0"),sQuery(id+"F0.wireOp",EDGE,"E7.4.1"),sQuery(id+"F0.wireOp",EDGE,"E7.5.0"),sQuery(id+"F0.wireOp",EDGE,"E7.5.1"),sQuery(id+"F0.wireOp",EDGE,"E7.6.0"),sQuery(id+"F0.wireOp",EDGE,"E7.6.1"),sQuery(id+"F0.wireOp",EDGE,"E7.7.0"),sQuery(id+"F0.wireOp",EDGE,"E7.7.1")])],"isStart":true});
            mirror(context, id + "F11", {"operationType" : NewBodyOperationType.ADD, "entities" : qUnion([Q0]), "mirrorPlane" : qUnion([Q1])});
        }
        {
            var Q0;
            Q0=makeQuery(id+"F7.opExtrude","CAP_FACE",FACE,{"disambiguationData":[OSD([sQuery(id+"F6.wireOp",EDGE,"E8.0"),sQuery(id+"F6.wireOp",EDGE,"E9.0"),sQuery(id+"F6.wireOp",EDGE,"E9.1"),sQuery(id+"F6.wireOp",EDGE,"E9.2"),sQuery(id+"F6.wireOp",EDGE,"E9.3"),sQuery(id+"F6.wireOp",EDGE,"E9.4"),sQuery(id+"F6.wireOp",EDGE,"E10.0"),sQuery(id+"F6.wireOp",EDGE,"E11.1.0"),sQuery(id+"F6.wireOp",EDGE,"E11.1.1"),sQuery(id+"F6.wireOp",EDGE,"E11.1.2"),sQuery(id+"F6.wireOp",EDGE,"E11.1.3"),sQuery(id+"F6.wireOp",EDGE,"E11.1.4"),sQuery(id+"F6.wireOp",EDGE,"E11.2.0"),sQuery(id+"F6.wireOp",EDGE,"E11.2.1"),sQuery(id+"F6.wireOp",EDGE,"E11.2.2"),sQuery(id+"F6.wireOp",EDGE,"E11.2.3"),sQuery(id+"F6.wireOp",EDGE,"E11.2.4"),sQuery(id+"F6.wireOp",EDGE,"E11.3.0"),sQuery(id+"F6.wireOp",EDGE,"E11.3.1"),sQuery(id+"F6.wireOp",EDGE,"E11.3.2"),sQuery(id+"F6.wireOp",EDGE,"E11.3.3"),sQuery(id+"F6.wireOp",EDGE,"E11.3.4"),sQuery(id+"F6.wireOp",EDGE,"E11.4.0"),sQuery(id+"F6.wireOp",EDGE,"E11.4.1"),sQuery(id+"F6.wireOp",EDGE,"E11.4.2"),sQuery(id+"F6.wireOp",EDGE,"E11.4.3"),sQuery(id+"F6.wireOp",EDGE,"E11.4.4"),sQuery(id+"F6.wireOp",EDGE,"E11.5.0"),sQuery(id+"F6.wireOp",EDGE,"E11.5.1"),sQuery(id+"F6.wireOp",EDGE,"E11.5.2"),sQuery(id+"F6.wireOp",EDGE,"E11.5.3"),sQuery(id+"F6.wireOp",EDGE,"E11.5.4"),sQuery(id+"F6.wireOp",EDGE,"E11.6.0"),sQuery(id+"F6.wireOp",EDGE,"E11.6.1"),sQuery(id+"F6.wireOp",EDGE,"E11.6.2"),sQuery(id+"F6.wireOp",EDGE,"E11.6.3"),sQuery(id+"F6.wireOp",EDGE,"E11.6.4"),sQuery(id+"F6.wireOp",EDGE,"E11.7.0"),sQuery(id+"F6.wireOp",EDGE,"E11.7.1"),sQuery(id+"F6.wireOp",EDGE,"E11.7.2"),sQuery(id+"F6.wireOp",EDGE,"E11.7.3"),sQuery(id+"F6.wireOp",EDGE,"E11.7.4")])],"isStart":false});
            var sketch = newSketch(context, id + "F12", { "sketchPlane" : qUnion([Q0])});
            skCircle(sketch, "E12", {"center": v(0, 0) * mm, "radius": 3 * mm});
            skSolve(sketch);
        }
        {
            var Q0;
            Q0 = qSketchRegion(id + "F12", true);
            extrude(context, id + "F13", {"entities" : qUnion([Q0]), "operationType" : NewBodyOperationType.REMOVE, "endBound" : BoundingType.THROUGH_ALL, "oppositeDirection" : true, "depth" : 25 * mm, "offsetDistance" : 25 * mm});
        }
        {
            var Q0;
            Q0=makeQuery(id+"F7.opExtrude","CAP_FACE",FACE,{"disambiguationData":[OSD([sQuery(id+"F6.wireOp",EDGE,"E8.0"),sQuery(id+"F6.wireOp",EDGE,"E9.0"),sQuery(id+"F6.wireOp",EDGE,"E9.1"),sQuery(id+"F6.wireOp",EDGE,"E9.2"),sQuery(id+"F6.wireOp",EDGE,"E9.3"),sQuery(id+"F6.wireOp",EDGE,"E9.4"),sQuery(id+"F6.wireOp",EDGE,"E10.0"),sQuery(id+"F6.wireOp",EDGE,"E11.1.0"),sQuery(id+"F6.wireOp",EDGE,"E11.1.1"),sQuery(id+"F6.wireOp",EDGE,"E11.1.2"),sQuery(id+"F6.wireOp",EDGE,"E11.1.3"),sQuery(id+"F6.wireOp",EDGE,"E11.1.4"),sQuery(id+"F6.wireOp",EDGE,"E11.2.0"),sQuery(id+"F6.wireOp",EDGE,"E11.2.1"),sQuery(id+"F6.wireOp",EDGE,"E11.2.2"),sQuery(id+"F6.wireOp",EDGE,"E11.2.3"),sQuery(id+"F6.wireOp",EDGE,"E11.2.4"),sQuery(id+"F6.wireOp",EDGE,"E11.3.0"),sQuery(id+"F6.wireOp",EDGE,"E11.3.1"),sQuery(id+"F6.wireOp",EDGE,"E11.3.2"),sQuery(id+"F6.wireOp",EDGE,"E11.3.3"),sQuery(id+"F6.wireOp",EDGE,"E11.3.4"),sQuery(id+"F6.wireOp",EDGE,"E11.4.0"),sQuery(id+"F6.wireOp",EDGE,"E11.4.1"),sQuery(id+"F6.wireOp",EDGE,"E11.4.2"),sQuery(id+"F6.wireOp",EDGE,"E11.4.3"),sQuery(id+"F6.wireOp",EDGE,"E11.4.4"),sQuery(id+"F6.wireOp",EDGE,"E11.5.0"),sQuery(id+"F6.wireOp",EDGE,"E11.5.1"),sQuery(id+"F6.wireOp",EDGE,"E11.5.2"),sQuery(id+"F6.wireOp",EDGE,"E11.5.3"),sQuery(id+"F6.wireOp",EDGE,"E11.5.4"),sQuery(id+"F6.wireOp",EDGE,"E11.6.0"),sQuery(id+"F6.wireOp",EDGE,"E11.6.1"),sQuery(id+"F6.wireOp",EDGE,"E11.6.2"),sQuery(id+"F6.wireOp",EDGE,"E11.6.3"),sQuery(id+"F6.wireOp",EDGE,"E11.6.4"),sQuery(id+"F6.wireOp",EDGE,"E11.7.0"),sQuery(id+"F6.wireOp",EDGE,"E11.7.1"),sQuery(id+"F6.wireOp",EDGE,"E11.7.2"),sQuery(id+"F6.wireOp",EDGE,"E11.7.3"),sQuery(id+"F6.wireOp",EDGE,"E11.7.4")])],"isStart":false});
            var sketch = newSketch(context, id + "F14", { "sketchPlane" : qUnion([Q0])});
            skArc(sketch, "E13.0", {"start": v(-42.36, 39.62) * mm, "mid": v(-46.78, 7.62) * mm, "end": v(-18.1, -7.25) * mm, "construction": true});
            skArc(sketch, "E14.0", {"start": v(-41.73, 40.28) * mm, "mid": v(-42.04, 39.95) * mm, "end": v(-42.36, 39.62) * mm, "construction": true});
            skArc(sketch, "E15.0", {"start": v(-30.63, 34.77) * mm, "mid": v(-34.16, 41.59) * mm, "end": v(-41.73, 40.28) * mm, "construction": true});
            skArc(sketch, "E16.0", {"start": v(-17.1, 4.14) * mm, "mid": v(-28.35, 17.47) * mm, "end": v(-30.63, 34.77) * mm, "construction": true});
            skArc(sketch, "E17.0", {"start": v(-18.1, -7.25) * mm, "mid": v(-14.2, -1.85) * mm, "end": v(-17.1, 4.14) * mm, "construction": true});
            skCircle(sketch, "E18.0", {"center": v(0, 0) * mm, "radius": 59 * mm});
            skArc(sketch, "E19.0", {"start": v(-17.57, -9.2) * mm, "mid": v(-12.23, -2.17) * mm, "end": v(-16, 5.8) * mm});
            skArc(sketch, "E19.1", {"start": v(-43.82, 40.99) * mm, "mid": v(-48.5, 6.6) * mm, "end": v(-17.57, -9.2) * mm});
            skArc(sketch, "E19.2", {"start": v(-16, 5.8) * mm, "mid": v(-26.53, 18.28) * mm, "end": v(-28.66, 34.46) * mm});
            skArc(sketch, "E19.3", {"start": v(-28.66, 34.46) * mm, "mid": v(-33.27, 43.38) * mm, "end": v(-43.17, 41.67) * mm});
            skArc(sketch, "E19.4", {"start": v(-43.17, 41.67) * mm, "mid": v(-43.5, 41.33) * mm, "end": v(-43.82, 40.99) * mm});
            skCircle(sketch, "E20", {"center": v(0, 0) * mm, "radius": 5 * mm});
            skArc(sketch, "E21.1.0", {"start": v(-15.42, -7.2) * mm, "mid": v(-31.68, -5.83) * mm, "end": v(-44.63, 4.1) * mm});
            skArc(sketch, "E21.1.1", {"start": v(-5.93, -18.92) * mm, "mid": v(-7.11, -10.18) * mm, "end": v(-15.42, -7.2) * mm});
            skArc(sketch, "E21.1.2", {"start": v(-59.97, -2) * mm, "mid": v(-38.95, -29.63) * mm, "end": v(-5.93, -18.92) * mm});
            skArc(sketch, "E21.1.3", {"start": v(-60, -1.06) * mm, "mid": v(-59.98, -1.53) * mm, "end": v(-59.97, -2) * mm});
            skArc(sketch, "E21.1.4", {"start": v(-44.63, 4.1) * mm, "mid": v(-54.2, 7.15) * mm, "end": v(-60, -1.06) * mm});
            skArc(sketch, "E21.2.0", {"start": v(-5.8, -16) * mm, "mid": v(-18.28, -26.53) * mm, "end": v(-34.46, -28.66) * mm});
            skArc(sketch, "E21.2.1", {"start": v(9.2, -17.57) * mm, "mid": v(2.17, -12.23) * mm, "end": v(-5.8, -16) * mm});
            skArc(sketch, "E21.2.2", {"start": v(-40.99, -43.82) * mm, "mid": v(-6.6, -48.5) * mm, "end": v(9.2, -17.57) * mm});
            skArc(sketch, "E21.2.3", {"start": v(-41.67, -43.17) * mm, "mid": v(-41.33, -43.5) * mm, "end": v(-40.99, -43.82) * mm});
            skArc(sketch, "E21.2.4", {"start": v(-34.46, -28.66) * mm, "mid": v(-43.38, -33.27) * mm, "end": v(-41.67, -43.17) * mm});
            skArc(sketch, "E21.3.0", {"start": v(7.2, -15.42) * mm, "mid": v(5.83, -31.68) * mm, "end": v(-4.1, -44.63) * mm});
            skArc(sketch, "E21.3.1", {"start": v(18.92, -5.93) * mm, "mid": v(10.18, -7.11) * mm, "end": v(7.2, -15.42) * mm});
            skArc(sketch, "E21.3.2", {"start": v(2, -59.97) * mm, "mid": v(29.63, -38.95) * mm, "end": v(18.92, -5.93) * mm});
            skArc(sketch, "E21.3.3", {"start": v(1.06, -60) * mm, "mid": v(1.53, -59.98) * mm, "end": v(2, -59.97) * mm});
            skArc(sketch, "E21.3.4", {"start": v(-4.1, -44.63) * mm, "mid": v(-7.15, -54.2) * mm, "end": v(1.06, -60) * mm});
            skArc(sketch, "E21.4.0", {"start": v(16, -5.8) * mm, "mid": v(26.53, -18.28) * mm, "end": v(28.66, -34.46) * mm});
            skArc(sketch, "E21.4.1", {"start": v(17.57, 9.2) * mm, "mid": v(12.23, 2.17) * mm, "end": v(16, -5.8) * mm});
            skArc(sketch, "E21.4.2", {"start": v(43.82, -40.99) * mm, "mid": v(48.5, -6.6) * mm, "end": v(17.57, 9.2) * mm});
            skArc(sketch, "E21.4.3", {"start": v(43.17, -41.67) * mm, "mid": v(43.5, -41.33) * mm, "end": v(43.82, -40.99) * mm});
            skArc(sketch, "E21.4.4", {"start": v(28.66, -34.46) * mm, "mid": v(33.27, -43.38) * mm, "end": v(43.17, -41.67) * mm});
            skArc(sketch, "E21.5.0", {"start": v(15.42, 7.2) * mm, "mid": v(31.68, 5.83) * mm, "end": v(44.63, -4.1) * mm});
            skArc(sketch, "E21.5.1", {"start": v(5.93, 18.92) * mm, "mid": v(7.11, 10.18) * mm, "end": v(15.42, 7.2) * mm});
            skArc(sketch, "E21.5.2", {"start": v(59.97, 2) * mm, "mid": v(38.95, 29.63) * mm, "end": v(5.93, 18.92) * mm});
            skArc(sketch, "E21.5.3", {"start": v(60, 1.06) * mm, "mid": v(59.98, 1.53) * mm, "end": v(59.97, 2) * mm});
            skArc(sketch, "E21.5.4", {"start": v(44.63, -4.1) * mm, "mid": v(54.2, -7.15) * mm, "end": v(60, 1.06) * mm});
            skArc(sketch, "E21.6.0", {"start": v(5.8, 16) * mm, "mid": v(18.28, 26.53) * mm, "end": v(34.46, 28.66) * mm});
            skArc(sketch, "E21.6.1", {"start": v(-9.2, 17.57) * mm, "mid": v(-2.17, 12.23) * mm, "end": v(5.8, 16) * mm});
            skArc(sketch, "E21.6.2", {"start": v(40.99, 43.82) * mm, "mid": v(6.6, 48.5) * mm, "end": v(-9.2, 17.57) * mm});
            skArc(sketch, "E21.6.3", {"start": v(41.67, 43.17) * mm, "mid": v(41.33, 43.5) * mm, "end": v(40.99, 43.82) * mm});
            skArc(sketch, "E21.6.4", {"start": v(34.46, 28.66) * mm, "mid": v(43.38, 33.27) * mm, "end": v(41.67, 43.17) * mm});
            skArc(sketch, "E21.7.0", {"start": v(-7.2, 15.42) * mm, "mid": v(-5.83, 31.68) * mm, "end": v(4.1, 44.63) * mm});
            skArc(sketch, "E21.7.1", {"start": v(-18.92, 5.93) * mm, "mid": v(-10.18, 7.11) * mm, "end": v(-7.2, 15.42) * mm});
            skArc(sketch, "E21.7.2", {"start": v(-2, 59.97) * mm, "mid": v(-29.63, 38.95) * mm, "end": v(-18.92, 5.93) * mm});
            skArc(sketch, "E21.7.3", {"start": v(-1.06, 60) * mm, "mid": v(-1.53, 59.98) * mm, "end": v(-2, 59.97) * mm});
            skArc(sketch, "E21.7.4", {"start": v(4.1, 44.63) * mm, "mid": v(7.15, 54.2) * mm, "end": v(-1.06, 60) * mm});
            skSolve(sketch);
        }
        {
            var Q0;
            {var subQ0=sQuery(id+"F14.wireOp",EDGE,"E19.3");var subQ1=sQuery(id+"F14.wireOp",EDGE,"E18.0");var subQ2=makeQuery(id+"F14.imprint","INTERSECT",VERTEX,{"derivedFrom":[subQ1,subQ0]});Q0=makeQuery(id+"F14.imprint","IMPRINT",FACE,{"disambiguationData":[TD([[makeQuery(id+"F14.imprint","IMPRINT",EDGE,{"disambiguationData":[TD([[subQ2,1.0]])],"derivedFrom":subQ1}),1.0]])]});}
            var Q1;
            {var subQ0=sQuery(id+"F14.wireOp",EDGE,"E21.6.2");var subQ1=sQuery(id+"F14.wireOp",EDGE,"E18.0");var subQ2=makeQuery(id+"F14.imprint","INTERSECT",VERTEX,{"derivedFrom":[subQ1,subQ0]});Q1=makeQuery(id+"F14.imprint","IMPRINT",FACE,{"disambiguationData":[TD([[makeQuery(id+"F14.imprint","IMPRINT",EDGE,{"disambiguationData":[TD([[subQ2,-1.0]])],"derivedFrom":subQ1}),1.0]])]});}
            var Q2;
            {var subQ0=sQuery(id+"F14.wireOp",EDGE,"E21.5.2");var subQ1=sQuery(id+"F14.wireOp",EDGE,"E18.0");var subQ2=makeQuery(id+"F14.imprint","INTERSECT",VERTEX,{"derivedFrom":[subQ1,subQ0]});Q2=makeQuery(id+"F14.imprint","IMPRINT",FACE,{"disambiguationData":[TD([[makeQuery(id+"F14.imprint","IMPRINT",EDGE,{"disambiguationData":[TD([[subQ2,-1.0]])],"derivedFrom":subQ1}),1.0]])]});}
            var Q3;
            {var subQ0=sQuery(id+"F14.wireOp",EDGE,"E21.4.2");var subQ1=sQuery(id+"F14.wireOp",EDGE,"E18.0");var subQ2=makeQuery(id+"F14.imprint","INTERSECT",VERTEX,{"derivedFrom":[subQ1,subQ0]});Q3=makeQuery(id+"F14.imprint","IMPRINT",FACE,{"disambiguationData":[TD([[makeQuery(id+"F14.imprint","IMPRINT",EDGE,{"disambiguationData":[TD([[subQ2,-1.0]])],"derivedFrom":subQ1}),1.0]])]});}
            var Q4;
            {var subQ0=sQuery(id+"F14.wireOp",EDGE,"E21.3.2");var subQ1=sQuery(id+"F14.wireOp",EDGE,"E18.0");var subQ2=makeQuery(id+"F14.imprint","INTERSECT",VERTEX,{"derivedFrom":[subQ1,subQ0]});Q4=makeQuery(id+"F14.imprint","IMPRINT",FACE,{"disambiguationData":[TD([[makeQuery(id+"F14.imprint","IMPRINT",EDGE,{"disambiguationData":[TD([[subQ2,-1.0]])],"derivedFrom":subQ1}),1.0]])]});}
            var Q5;
            {var subQ0=sQuery(id+"F14.wireOp",EDGE,"E21.2.2");var subQ1=sQuery(id+"F14.wireOp",EDGE,"E18.0");var subQ2=makeQuery(id+"F14.imprint","INTERSECT",VERTEX,{"derivedFrom":[subQ1,subQ0]});Q5=makeQuery(id+"F14.imprint","IMPRINT",FACE,{"disambiguationData":[TD([[makeQuery(id+"F14.imprint","IMPRINT",EDGE,{"disambiguationData":[TD([[subQ2,-1.0]])],"derivedFrom":subQ1}),1.0]])]});}
            var Q6;
            {var subQ0=sQuery(id+"F14.wireOp",EDGE,"E21.1.2");var subQ1=sQuery(id+"F14.wireOp",EDGE,"E18.0");var subQ2=makeQuery(id+"F14.imprint","INTERSECT",VERTEX,{"derivedFrom":[subQ1,subQ0]});Q6=makeQuery(id+"F14.imprint","IMPRINT",FACE,{"disambiguationData":[TD([[makeQuery(id+"F14.imprint","IMPRINT",EDGE,{"disambiguationData":[TD([[subQ2,-1.0]])],"derivedFrom":subQ1}),1.0]])]});}
            var Q7;
            {var subQ0=sQuery(id+"F14.wireOp",EDGE,"E19.1");var subQ1=sQuery(id+"F14.wireOp",EDGE,"E18.0");var subQ2=makeQuery(id+"F14.imprint","INTERSECT",VERTEX,{"derivedFrom":[subQ1,subQ0]});Q7=makeQuery(id+"F14.imprint","IMPRINT",FACE,{"disambiguationData":[TD([[makeQuery(id+"F14.imprint","IMPRINT",EDGE,{"disambiguationData":[TD([[subQ2,-1.0]])],"derivedFrom":subQ1}),1.0]])]});}
            extrude(context, id + "F15", {"entities" : qUnion([Q0, Q1, Q2, Q3, Q4, Q5, Q6, Q7]), "operationType" : NewBodyOperationType.REMOVE, "endBound" : BoundingType.THROUGH_ALL, "oppositeDirection" : true, "depth" : 25 * mm, "offsetDistance" : 25 * mm});
        }
        {
            var Q0;
            Q0=makeQuery(id+"F14.imprint","IMPRINT",FACE,{"disambiguationData":[TD([[makeQuery(id+"F14.imprint","IMPRINT",EDGE,{"derivedFrom":sQuery(id+"F14.wireOp",EDGE,"E20")}),-1.0]])]});
            extrude(context, id + "F16", {"entities" : qUnion([Q0]), "operationType" : NewBodyOperationType.REMOVE, "oppositeDirection" : true, "depth" : 16 * mm, "offsetDistance" : 25 * mm});
        }
    });
